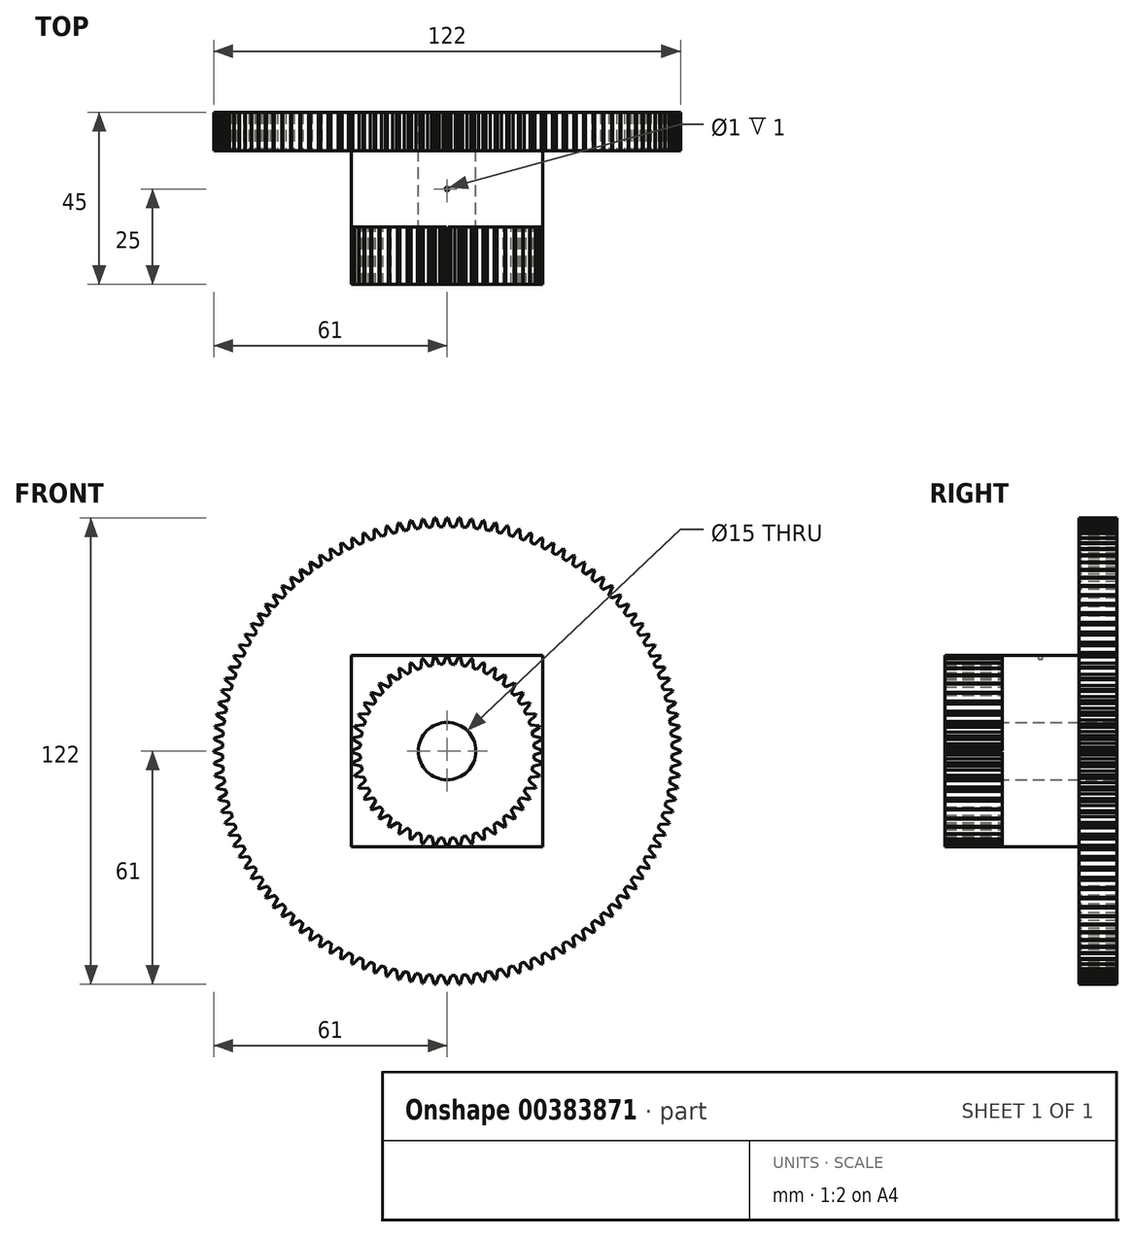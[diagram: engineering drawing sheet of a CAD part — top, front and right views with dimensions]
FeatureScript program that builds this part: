
annotation { "Feature Type Name" : "Feature", "Feature Type Description" : "" }
export const myFeature = defineFeature(function(context is Context, id is Id, definition is map)
    precondition{}
    {
        {
            var Q0;
            Q0=qCreatedBy(makeId("Front.planeOp"),FACE);
            var sketch = newSketch(context, id + "F0", { "sketchPlane" : qUnion([Q0])});
            skCircle(sketch, "E0", {"center": v(0, 0) * mm, "radius": 7.5 * mm});
            skCircle(sketch, "E1", {"center": v(0, 0) * mm, "radius": 22.75 * mm});
            skCircle(sketch, "E2", {"center": v(0, 0) * mm, "radius": 25 * mm, "construction": true});
            skLineSegment(sketch, "E3", {"start": v(-1.01, 22.73) * mm, "end": v(-0.19, 25) * mm});
            skLineSegment(sketch, "E4", {"start": v(-0.19, 25) * mm, "end": v(0, 25) * mm});
            skLineSegment(sketch, "E5", {"start": v(-1.01, 22.73) * mm, "end": v(-1.01, 25.94) * mm, "construction": true});
            skLineSegment(sketch, "E6.MirrorCS", {"start": v(0.19, 25) * mm, "end": v(0, 25) * mm});
            skLineSegment(sketch, "E7.MirrorCS", {"start": v(1.01, 22.73) * mm, "end": v(0.19, 25) * mm});
            skLineSegment(sketch, "E8.1.0", {"start": v(-3.97, 22.4) * mm, "end": v(-3.45, 24.76) * mm});
            skLineSegment(sketch, "E8.1.1", {"start": v(-3.45, 24.76) * mm, "end": v(-3.26, 24.79) * mm});
            skLineSegment(sketch, "E8.1.2", {"start": v(-3.08, 24.81) * mm, "end": v(-3.26, 24.79) * mm});
            skLineSegment(sketch, "E8.1.3", {"start": v(-1.96, 22.67) * mm, "end": v(-3.08, 24.81) * mm});
            skLineSegment(sketch, "E8.2.0", {"start": v(-6.86, 21.7) * mm, "end": v(-6.65, 24.1) * mm});
            skLineSegment(sketch, "E8.2.1", {"start": v(-6.65, 24.1) * mm, "end": v(-6.47, 24.15) * mm});
            skLineSegment(sketch, "E8.2.2", {"start": v(-6.29, 24.2) * mm, "end": v(-6.47, 24.15) * mm});
            skLineSegment(sketch, "E8.2.3", {"start": v(-4.9, 22.22) * mm, "end": v(-6.29, 24.2) * mm});
            skLineSegment(sketch, "E8.3.0", {"start": v(-9.63, 20.6) * mm, "end": v(-9.74, 23.03) * mm});
            skLineSegment(sketch, "E8.3.1", {"start": v(-9.74, 23.03) * mm, "end": v(-9.57, 23.1) * mm});
            skLineSegment(sketch, "E8.3.2", {"start": v(-9.4, 23.17) * mm, "end": v(-9.57, 23.1) * mm});
            skLineSegment(sketch, "E8.3.3", {"start": v(-7.76, 21.39) * mm, "end": v(-9.4, 23.17) * mm});
            skLineSegment(sketch, "E8.4.0", {"start": v(-12.24, 19.18) * mm, "end": v(-12.66, 21.56) * mm});
            skLineSegment(sketch, "E8.4.1", {"start": v(-12.66, 21.56) * mm, "end": v(-12.5, 21.65) * mm});
            skLineSegment(sketch, "E8.4.2", {"start": v(-12.34, 21.74) * mm, "end": v(-12.5, 21.65) * mm});
            skLineSegment(sketch, "E8.4.3", {"start": v(-10.48, 20.19) * mm, "end": v(-12.34, 21.74) * mm});
            skLineSegment(sketch, "E8.5.0", {"start": v(-14.64, 17.41) * mm, "end": v(-15.37, 19.72) * mm});
            skLineSegment(sketch, "E8.5.1", {"start": v(-15.37, 19.72) * mm, "end": v(-15.22, 19.83) * mm});
            skLineSegment(sketch, "E8.5.2", {"start": v(-15.07, 19.95) * mm, "end": v(-15.22, 19.83) * mm});
            skLineSegment(sketch, "E8.5.3", {"start": v(-13.03, 18.65) * mm, "end": v(-15.07, 19.95) * mm});
            skLineSegment(sketch, "E8.6.0", {"start": v(-16.79, 15.35) * mm, "end": v(-17.81, 17.55) * mm});
            skLineSegment(sketch, "E8.6.1", {"start": v(-17.81, 17.55) * mm, "end": v(-17.68, 17.68) * mm});
            skLineSegment(sketch, "E8.6.2", {"start": v(-17.55, 17.81) * mm, "end": v(-17.68, 17.68) * mm});
            skLineSegment(sketch, "E8.6.3", {"start": v(-15.35, 16.79) * mm, "end": v(-17.55, 17.81) * mm});
            skLineSegment(sketch, "E8.7.0", {"start": v(-18.65, 13.03) * mm, "end": v(-19.95, 15.07) * mm});
            skLineSegment(sketch, "E8.7.1", {"start": v(-19.95, 15.07) * mm, "end": v(-19.83, 15.22) * mm});
            skLineSegment(sketch, "E8.7.2", {"start": v(-19.72, 15.37) * mm, "end": v(-19.83, 15.22) * mm});
            skLineSegment(sketch, "E8.7.3", {"start": v(-17.41, 14.64) * mm, "end": v(-19.72, 15.37) * mm});
            skLineSegment(sketch, "E8.8.0", {"start": v(-20.19, 10.48) * mm, "end": v(-21.74, 12.34) * mm});
            skLineSegment(sketch, "E8.8.1", {"start": v(-21.74, 12.34) * mm, "end": v(-21.65, 12.5) * mm});
            skLineSegment(sketch, "E8.8.2", {"start": v(-21.56, 12.66) * mm, "end": v(-21.65, 12.5) * mm});
            skLineSegment(sketch, "E8.8.3", {"start": v(-19.18, 12.24) * mm, "end": v(-21.56, 12.66) * mm});
            skLineSegment(sketch, "E8.9.0", {"start": v(-21.39, 7.76) * mm, "end": v(-23.17, 9.4) * mm});
            skLineSegment(sketch, "E8.9.1", {"start": v(-23.17, 9.4) * mm, "end": v(-23.1, 9.57) * mm});
            skLineSegment(sketch, "E8.9.2", {"start": v(-23.03, 9.74) * mm, "end": v(-23.1, 9.57) * mm});
            skLineSegment(sketch, "E8.9.3", {"start": v(-20.6, 9.63) * mm, "end": v(-23.03, 9.74) * mm});
            skLineSegment(sketch, "E8.10.0", {"start": v(-22.22, 4.9) * mm, "end": v(-24.2, 6.29) * mm});
            skLineSegment(sketch, "E8.10.1", {"start": v(-24.2, 6.29) * mm, "end": v(-24.15, 6.47) * mm});
            skLineSegment(sketch, "E8.10.2", {"start": v(-24.1, 6.65) * mm, "end": v(-24.15, 6.47) * mm});
            skLineSegment(sketch, "E8.10.3", {"start": v(-21.7, 6.86) * mm, "end": v(-24.1, 6.65) * mm});
            skLineSegment(sketch, "E8.11.0", {"start": v(-22.67, 1.96) * mm, "end": v(-24.81, 3.08) * mm});
            skLineSegment(sketch, "E8.11.1", {"start": v(-24.81, 3.08) * mm, "end": v(-24.79, 3.26) * mm});
            skLineSegment(sketch, "E8.11.2", {"start": v(-24.76, 3.45) * mm, "end": v(-24.79, 3.26) * mm});
            skLineSegment(sketch, "E8.11.3", {"start": v(-22.4, 3.97) * mm, "end": v(-24.76, 3.45) * mm});
            skLineSegment(sketch, "E9.1.12.0", {"start": v(-22.73, -1.01) * mm, "end": v(-25, -0.19) * mm});
            skLineSegment(sketch, "E9.3.12.0", {"start": v(-25, -0.19) * mm, "end": v(-25, 0) * mm});
            skLineSegment(sketch, "E9.6.12.0", {"start": v(-25, 0.19) * mm, "end": v(-25, 0) * mm});
            skLineSegment(sketch, "E9.9.12.0", {"start": v(-22.73, 1.01) * mm, "end": v(-25, 0.19) * mm});
            skLineSegment(sketch, "E9.1.13.0", {"start": v(-22.4, -3.97) * mm, "end": v(-24.76, -3.45) * mm});
            skLineSegment(sketch, "E9.3.13.0", {"start": v(-24.76, -3.45) * mm, "end": v(-24.79, -3.26) * mm});
            skLineSegment(sketch, "E9.6.13.0", {"start": v(-24.81, -3.08) * mm, "end": v(-24.79, -3.26) * mm});
            skLineSegment(sketch, "E9.9.13.0", {"start": v(-22.67, -1.96) * mm, "end": v(-24.81, -3.08) * mm});
            skLineSegment(sketch, "E9.1.14.0", {"start": v(-21.7, -6.86) * mm, "end": v(-24.1, -6.65) * mm});
            skLineSegment(sketch, "E9.3.14.0", {"start": v(-24.1, -6.65) * mm, "end": v(-24.15, -6.47) * mm});
            skLineSegment(sketch, "E9.6.14.0", {"start": v(-24.2, -6.29) * mm, "end": v(-24.15, -6.47) * mm});
            skLineSegment(sketch, "E9.9.14.0", {"start": v(-22.22, -4.9) * mm, "end": v(-24.2, -6.29) * mm});
            skLineSegment(sketch, "E9.1.15.0", {"start": v(-20.6, -9.63) * mm, "end": v(-23.03, -9.74) * mm});
            skLineSegment(sketch, "E9.3.15.0", {"start": v(-23.03, -9.74) * mm, "end": v(-23.1, -9.57) * mm});
            skLineSegment(sketch, "E9.6.15.0", {"start": v(-23.17, -9.4) * mm, "end": v(-23.1, -9.57) * mm});
            skLineSegment(sketch, "E9.9.15.0", {"start": v(-21.39, -7.76) * mm, "end": v(-23.17, -9.4) * mm});
            skLineSegment(sketch, "E9.1.16.0", {"start": v(-19.18, -12.24) * mm, "end": v(-21.56, -12.66) * mm});
            skLineSegment(sketch, "E9.3.16.0", {"start": v(-21.56, -12.66) * mm, "end": v(-21.65, -12.5) * mm});
            skLineSegment(sketch, "E9.6.16.0", {"start": v(-21.74, -12.34) * mm, "end": v(-21.65, -12.5) * mm});
            skLineSegment(sketch, "E9.9.16.0", {"start": v(-20.19, -10.48) * mm, "end": v(-21.74, -12.34) * mm});
            skLineSegment(sketch, "E9.1.17.0", {"start": v(-17.41, -14.64) * mm, "end": v(-19.72, -15.37) * mm});
            skLineSegment(sketch, "E9.3.17.0", {"start": v(-19.72, -15.37) * mm, "end": v(-19.83, -15.22) * mm});
            skLineSegment(sketch, "E9.6.17.0", {"start": v(-19.95, -15.07) * mm, "end": v(-19.83, -15.22) * mm});
            skLineSegment(sketch, "E9.9.17.0", {"start": v(-18.65, -13.03) * mm, "end": v(-19.95, -15.07) * mm});
            skLineSegment(sketch, "E9.1.18.0", {"start": v(-15.35, -16.79) * mm, "end": v(-17.55, -17.81) * mm});
            skLineSegment(sketch, "E9.3.18.0", {"start": v(-17.55, -17.81) * mm, "end": v(-17.68, -17.68) * mm});
            skLineSegment(sketch, "E9.6.18.0", {"start": v(-17.81, -17.55) * mm, "end": v(-17.68, -17.68) * mm});
            skLineSegment(sketch, "E9.9.18.0", {"start": v(-16.79, -15.35) * mm, "end": v(-17.81, -17.55) * mm});
            skLineSegment(sketch, "E9.1.19.0", {"start": v(-13.03, -18.65) * mm, "end": v(-15.07, -19.95) * mm});
            skLineSegment(sketch, "E9.3.19.0", {"start": v(-15.07, -19.95) * mm, "end": v(-15.22, -19.83) * mm});
            skLineSegment(sketch, "E9.6.19.0", {"start": v(-15.37, -19.72) * mm, "end": v(-15.22, -19.83) * mm});
            skLineSegment(sketch, "E9.9.19.0", {"start": v(-14.64, -17.41) * mm, "end": v(-15.37, -19.72) * mm});
            skLineSegment(sketch, "E9.1.20.0", {"start": v(-10.48, -20.19) * mm, "end": v(-12.34, -21.74) * mm});
            skLineSegment(sketch, "E9.3.20.0", {"start": v(-12.34, -21.74) * mm, "end": v(-12.5, -21.65) * mm});
            skLineSegment(sketch, "E9.6.20.0", {"start": v(-12.66, -21.56) * mm, "end": v(-12.5, -21.65) * mm});
            skLineSegment(sketch, "E9.9.20.0", {"start": v(-12.24, -19.18) * mm, "end": v(-12.66, -21.56) * mm});
            skLineSegment(sketch, "E9.1.21.0", {"start": v(-7.76, -21.39) * mm, "end": v(-9.4, -23.17) * mm});
            skLineSegment(sketch, "E9.3.21.0", {"start": v(-9.4, -23.17) * mm, "end": v(-9.57, -23.1) * mm});
            skLineSegment(sketch, "E9.6.21.0", {"start": v(-9.74, -23.03) * mm, "end": v(-9.57, -23.1) * mm});
            skLineSegment(sketch, "E9.9.21.0", {"start": v(-9.63, -20.6) * mm, "end": v(-9.74, -23.03) * mm});
            skLineSegment(sketch, "E9.1.22.0", {"start": v(-4.9, -22.22) * mm, "end": v(-6.29, -24.2) * mm});
            skLineSegment(sketch, "E9.3.22.0", {"start": v(-6.29, -24.2) * mm, "end": v(-6.47, -24.15) * mm});
            skLineSegment(sketch, "E9.6.22.0", {"start": v(-6.65, -24.1) * mm, "end": v(-6.47, -24.15) * mm});
            skLineSegment(sketch, "E9.9.22.0", {"start": v(-6.86, -21.7) * mm, "end": v(-6.65, -24.1) * mm});
            skLineSegment(sketch, "E9.1.23.0", {"start": v(-1.96, -22.67) * mm, "end": v(-3.08, -24.81) * mm});
            skLineSegment(sketch, "E9.3.23.0", {"start": v(-3.08, -24.81) * mm, "end": v(-3.26, -24.79) * mm});
            skLineSegment(sketch, "E9.6.23.0", {"start": v(-3.45, -24.76) * mm, "end": v(-3.26, -24.79) * mm});
            skLineSegment(sketch, "E9.9.23.0", {"start": v(-3.97, -22.4) * mm, "end": v(-3.45, -24.76) * mm});
            skLineSegment(sketch, "E10.1.24.0", {"start": v(1.01, -22.73) * mm, "end": v(0.19, -25) * mm});
            skLineSegment(sketch, "E10.3.24.0", {"start": v(0.19, -25) * mm, "end": v(0, -25) * mm});
            skLineSegment(sketch, "E10.6.24.0", {"start": v(-0.19, -25) * mm, "end": v(0, -25) * mm});
            skLineSegment(sketch, "E10.9.24.0", {"start": v(-1.01, -22.73) * mm, "end": v(-0.19, -25) * mm});
            skLineSegment(sketch, "E10.1.25.0", {"start": v(3.97, -22.4) * mm, "end": v(3.45, -24.76) * mm});
            skLineSegment(sketch, "E10.3.25.0", {"start": v(3.45, -24.76) * mm, "end": v(3.26, -24.79) * mm});
            skLineSegment(sketch, "E10.6.25.0", {"start": v(3.08, -24.81) * mm, "end": v(3.26, -24.79) * mm});
            skLineSegment(sketch, "E10.9.25.0", {"start": v(1.96, -22.67) * mm, "end": v(3.08, -24.81) * mm});
            skLineSegment(sketch, "E10.1.26.0", {"start": v(6.86, -21.7) * mm, "end": v(6.65, -24.1) * mm});
            skLineSegment(sketch, "E10.3.26.0", {"start": v(6.65, -24.1) * mm, "end": v(6.47, -24.15) * mm});
            skLineSegment(sketch, "E10.6.26.0", {"start": v(6.29, -24.2) * mm, "end": v(6.47, -24.15) * mm});
            skLineSegment(sketch, "E10.9.26.0", {"start": v(4.9, -22.22) * mm, "end": v(6.29, -24.2) * mm});
            skLineSegment(sketch, "E10.1.27.0", {"start": v(9.63, -20.6) * mm, "end": v(9.74, -23.03) * mm});
            skLineSegment(sketch, "E10.3.27.0", {"start": v(9.74, -23.03) * mm, "end": v(9.57, -23.1) * mm});
            skLineSegment(sketch, "E10.6.27.0", {"start": v(9.4, -23.17) * mm, "end": v(9.57, -23.1) * mm});
            skLineSegment(sketch, "E10.9.27.0", {"start": v(7.76, -21.39) * mm, "end": v(9.4, -23.17) * mm});
            skLineSegment(sketch, "E10.1.28.0", {"start": v(12.24, -19.18) * mm, "end": v(12.66, -21.56) * mm});
            skLineSegment(sketch, "E10.3.28.0", {"start": v(12.66, -21.56) * mm, "end": v(12.5, -21.65) * mm});
            skLineSegment(sketch, "E10.6.28.0", {"start": v(12.34, -21.74) * mm, "end": v(12.5, -21.65) * mm});
            skLineSegment(sketch, "E10.9.28.0", {"start": v(10.48, -20.19) * mm, "end": v(12.34, -21.74) * mm});
            skLineSegment(sketch, "E10.1.29.0", {"start": v(14.64, -17.41) * mm, "end": v(15.37, -19.72) * mm});
            skLineSegment(sketch, "E10.3.29.0", {"start": v(15.37, -19.72) * mm, "end": v(15.22, -19.83) * mm});
            skLineSegment(sketch, "E10.6.29.0", {"start": v(15.07, -19.95) * mm, "end": v(15.22, -19.83) * mm});
            skLineSegment(sketch, "E10.9.29.0", {"start": v(13.03, -18.65) * mm, "end": v(15.07, -19.95) * mm});
            skLineSegment(sketch, "E10.1.30.0", {"start": v(16.79, -15.35) * mm, "end": v(17.81, -17.55) * mm});
            skLineSegment(sketch, "E10.3.30.0", {"start": v(17.81, -17.55) * mm, "end": v(17.68, -17.68) * mm});
            skLineSegment(sketch, "E10.6.30.0", {"start": v(17.55, -17.81) * mm, "end": v(17.68, -17.68) * mm});
            skLineSegment(sketch, "E10.9.30.0", {"start": v(15.35, -16.79) * mm, "end": v(17.55, -17.81) * mm});
            skLineSegment(sketch, "E10.1.31.0", {"start": v(18.65, -13.03) * mm, "end": v(19.95, -15.07) * mm});
            skLineSegment(sketch, "E10.3.31.0", {"start": v(19.95, -15.07) * mm, "end": v(19.83, -15.22) * mm});
            skLineSegment(sketch, "E10.6.31.0", {"start": v(19.72, -15.37) * mm, "end": v(19.83, -15.22) * mm});
            skLineSegment(sketch, "E10.9.31.0", {"start": v(17.41, -14.64) * mm, "end": v(19.72, -15.37) * mm});
            skLineSegment(sketch, "E10.1.32.0", {"start": v(20.19, -10.48) * mm, "end": v(21.74, -12.34) * mm});
            skLineSegment(sketch, "E10.3.32.0", {"start": v(21.74, -12.34) * mm, "end": v(21.65, -12.5) * mm});
            skLineSegment(sketch, "E10.6.32.0", {"start": v(21.56, -12.66) * mm, "end": v(21.65, -12.5) * mm});
            skLineSegment(sketch, "E10.9.32.0", {"start": v(19.18, -12.24) * mm, "end": v(21.56, -12.66) * mm});
            skLineSegment(sketch, "E10.1.33.0", {"start": v(21.39, -7.76) * mm, "end": v(23.17, -9.4) * mm});
            skLineSegment(sketch, "E10.3.33.0", {"start": v(23.17, -9.4) * mm, "end": v(23.1, -9.57) * mm});
            skLineSegment(sketch, "E10.6.33.0", {"start": v(23.03, -9.74) * mm, "end": v(23.1, -9.57) * mm});
            skLineSegment(sketch, "E10.9.33.0", {"start": v(20.6, -9.63) * mm, "end": v(23.03, -9.74) * mm});
            skLineSegment(sketch, "E10.1.34.0", {"start": v(22.22, -4.9) * mm, "end": v(24.2, -6.29) * mm});
            skLineSegment(sketch, "E10.3.34.0", {"start": v(24.2, -6.29) * mm, "end": v(24.15, -6.47) * mm});
            skLineSegment(sketch, "E10.6.34.0", {"start": v(24.1, -6.65) * mm, "end": v(24.15, -6.47) * mm});
            skLineSegment(sketch, "E10.9.34.0", {"start": v(21.7, -6.86) * mm, "end": v(24.1, -6.65) * mm});
            skLineSegment(sketch, "E10.1.35.0", {"start": v(22.67, -1.96) * mm, "end": v(24.81, -3.08) * mm});
            skLineSegment(sketch, "E10.3.35.0", {"start": v(24.81, -3.08) * mm, "end": v(24.79, -3.26) * mm});
            skLineSegment(sketch, "E10.6.35.0", {"start": v(24.76, -3.45) * mm, "end": v(24.79, -3.26) * mm});
            skLineSegment(sketch, "E10.9.35.0", {"start": v(22.4, -3.97) * mm, "end": v(24.76, -3.45) * mm});
            skLineSegment(sketch, "E11.1.36.0", {"start": v(22.73, 1.01) * mm, "end": v(25, 0.19) * mm});
            skLineSegment(sketch, "E11.3.36.0", {"start": v(25, 0.19) * mm, "end": v(25, 0) * mm});
            skLineSegment(sketch, "E11.6.36.0", {"start": v(25, -0.19) * mm, "end": v(25, 0) * mm});
            skLineSegment(sketch, "E11.9.36.0", {"start": v(22.73, -1.01) * mm, "end": v(25, -0.19) * mm});
            skLineSegment(sketch, "E11.1.37.0", {"start": v(22.4, 3.97) * mm, "end": v(24.76, 3.45) * mm});
            skLineSegment(sketch, "E11.3.37.0", {"start": v(24.76, 3.45) * mm, "end": v(24.79, 3.26) * mm});
            skLineSegment(sketch, "E11.6.37.0", {"start": v(24.81, 3.08) * mm, "end": v(24.79, 3.26) * mm});
            skLineSegment(sketch, "E11.9.37.0", {"start": v(22.67, 1.96) * mm, "end": v(24.81, 3.08) * mm});
            skLineSegment(sketch, "E11.1.38.0", {"start": v(21.7, 6.86) * mm, "end": v(24.1, 6.65) * mm});
            skLineSegment(sketch, "E11.3.38.0", {"start": v(24.1, 6.65) * mm, "end": v(24.15, 6.47) * mm});
            skLineSegment(sketch, "E11.6.38.0", {"start": v(24.2, 6.29) * mm, "end": v(24.15, 6.47) * mm});
            skLineSegment(sketch, "E11.9.38.0", {"start": v(22.22, 4.9) * mm, "end": v(24.2, 6.29) * mm});
            skLineSegment(sketch, "E11.1.39.0", {"start": v(20.6, 9.63) * mm, "end": v(23.03, 9.74) * mm});
            skLineSegment(sketch, "E11.3.39.0", {"start": v(23.03, 9.74) * mm, "end": v(23.1, 9.57) * mm});
            skLineSegment(sketch, "E11.6.39.0", {"start": v(23.17, 9.4) * mm, "end": v(23.1, 9.57) * mm});
            skLineSegment(sketch, "E11.9.39.0", {"start": v(21.39, 7.76) * mm, "end": v(23.17, 9.4) * mm});
            skLineSegment(sketch, "E11.1.40.0", {"start": v(19.18, 12.24) * mm, "end": v(21.56, 12.66) * mm});
            skLineSegment(sketch, "E11.3.40.0", {"start": v(21.56, 12.66) * mm, "end": v(21.65, 12.5) * mm});
            skLineSegment(sketch, "E11.6.40.0", {"start": v(21.74, 12.34) * mm, "end": v(21.65, 12.5) * mm});
            skLineSegment(sketch, "E11.9.40.0", {"start": v(20.19, 10.48) * mm, "end": v(21.74, 12.34) * mm});
            skLineSegment(sketch, "E11.1.41.0", {"start": v(17.41, 14.64) * mm, "end": v(19.72, 15.37) * mm});
            skLineSegment(sketch, "E11.3.41.0", {"start": v(19.72, 15.37) * mm, "end": v(19.83, 15.22) * mm});
            skLineSegment(sketch, "E11.6.41.0", {"start": v(19.95, 15.07) * mm, "end": v(19.83, 15.22) * mm});
            skLineSegment(sketch, "E11.9.41.0", {"start": v(18.65, 13.03) * mm, "end": v(19.95, 15.07) * mm});
            skLineSegment(sketch, "E11.1.42.0", {"start": v(15.35, 16.79) * mm, "end": v(17.55, 17.81) * mm});
            skLineSegment(sketch, "E11.3.42.0", {"start": v(17.55, 17.81) * mm, "end": v(17.68, 17.68) * mm});
            skLineSegment(sketch, "E11.6.42.0", {"start": v(17.81, 17.55) * mm, "end": v(17.68, 17.68) * mm});
            skLineSegment(sketch, "E11.9.42.0", {"start": v(16.79, 15.35) * mm, "end": v(17.81, 17.55) * mm});
            skLineSegment(sketch, "E11.1.43.0", {"start": v(13.03, 18.65) * mm, "end": v(15.07, 19.95) * mm});
            skLineSegment(sketch, "E11.3.43.0", {"start": v(15.07, 19.95) * mm, "end": v(15.22, 19.83) * mm});
            skLineSegment(sketch, "E11.6.43.0", {"start": v(15.37, 19.72) * mm, "end": v(15.22, 19.83) * mm});
            skLineSegment(sketch, "E11.9.43.0", {"start": v(14.64, 17.41) * mm, "end": v(15.37, 19.72) * mm});
            skLineSegment(sketch, "E11.1.44.0", {"start": v(10.48, 20.19) * mm, "end": v(12.34, 21.74) * mm});
            skLineSegment(sketch, "E11.3.44.0", {"start": v(12.34, 21.74) * mm, "end": v(12.5, 21.65) * mm});
            skLineSegment(sketch, "E11.6.44.0", {"start": v(12.66, 21.56) * mm, "end": v(12.5, 21.65) * mm});
            skLineSegment(sketch, "E11.9.44.0", {"start": v(12.24, 19.18) * mm, "end": v(12.66, 21.56) * mm});
            skLineSegment(sketch, "E11.1.45.0", {"start": v(7.76, 21.39) * mm, "end": v(9.4, 23.17) * mm});
            skLineSegment(sketch, "E11.3.45.0", {"start": v(9.4, 23.17) * mm, "end": v(9.57, 23.1) * mm});
            skLineSegment(sketch, "E11.6.45.0", {"start": v(9.74, 23.03) * mm, "end": v(9.57, 23.1) * mm});
            skLineSegment(sketch, "E11.9.45.0", {"start": v(9.63, 20.6) * mm, "end": v(9.74, 23.03) * mm});
            skLineSegment(sketch, "E11.1.46.0", {"start": v(4.9, 22.22) * mm, "end": v(6.29, 24.2) * mm});
            skLineSegment(sketch, "E11.3.46.0", {"start": v(6.29, 24.2) * mm, "end": v(6.47, 24.15) * mm});
            skLineSegment(sketch, "E11.6.46.0", {"start": v(6.65, 24.1) * mm, "end": v(6.47, 24.15) * mm});
            skLineSegment(sketch, "E11.9.46.0", {"start": v(6.86, 21.7) * mm, "end": v(6.65, 24.1) * mm});
            skLineSegment(sketch, "E11.1.47.0", {"start": v(1.96, 22.67) * mm, "end": v(3.08, 24.81) * mm});
            skLineSegment(sketch, "E11.3.47.0", {"start": v(3.08, 24.81) * mm, "end": v(3.26, 24.79) * mm});
            skLineSegment(sketch, "E11.6.47.0", {"start": v(3.45, 24.76) * mm, "end": v(3.26, 24.79) * mm});
            skLineSegment(sketch, "E11.9.47.0", {"start": v(3.97, 22.4) * mm, "end": v(3.45, 24.76) * mm});
            skSolve(sketch);
        }
        {
            var Q0;
            Q0=qSketchRegion(id+"F0",true);
            extrude(context, id + "F1", {"entities" : qUnion([Q0]), "depth" : 15 * mm});
        }
        {
            var Q0;
            Q0=qCreatedBy(makeId("Front.planeOp"),FACE);
            var sketch = newSketch(context, id + "F2", { "sketchPlane" : qUnion([Q0])});
            skCircle(sketch, "E12", {"center": v(0, 0) * mm, "radius": 7.5 * mm});
            skLineSegment(sketch, "E13.bottom", {"start": v(-25, -25) * mm, "end": v(25, -25) * mm});
            skLineSegment(sketch, "E13.top", {"start": v(-25, 25) * mm, "end": v(25, 25) * mm});
            skLineSegment(sketch, "E13.left", {"start": v(-25, -25) * mm, "end": v(-25, 25) * mm});
            skLineSegment(sketch, "E13.right", {"start": v(25, -25) * mm, "end": v(25, 25) * mm});
            skSolve(sketch);
        }
        {
            var Q0;
            Q0=qSketchRegion(id+"F2",true);
            extrude(context, id + "F3", {"entities" : qUnion([Q0]), "operationType" : NewBodyOperationType.ADD, "depth" : -20 * mm});
        }
        {
            var Q0;
            Q0=makeQuery(id+"F3.opExtrude","CAP_FACE",FACE,{"disambiguationData":[OSD([sQuery(id+"F2.wireOp",EDGE,"Zh5lLQ9h-1iR5-KiPg-C2Wr-JR3NM9Zv75rL"),sQuery(id+"F2.wireOp",EDGE,"E12")])],"isStart":false});
            var sketch = newSketch(context, id + "F4", { "sketchPlane" : qUnion([Q0])});
            skCircle(sketch, "E14", {"center": v(0, 0) * mm, "radius": 58.75 * mm});
            skCircle(sketch, "E15", {"center": v(0, 0) * mm, "radius": 61 * mm, "construction": true});
            skLineSegment(sketch, "E16", {"start": v(-1, 58.74) * mm, "end": v(-1, 64.16) * mm, "construction": true});
            skLineSegment(sketch, "E17", {"start": v(-1, 58.74) * mm, "end": v(-0.19, 61) * mm});
            skLineSegment(sketch, "E18", {"start": v(-0.19, 61) * mm, "end": v(0, 61) * mm});
            skLineSegment(sketch, "E19.MirrorCS", {"start": v(0.19, 61) * mm, "end": v(0, 61) * mm});
            skLineSegment(sketch, "E20.MirrorCS", {"start": v(1, 58.74) * mm, "end": v(0.19, 61) * mm});
            skLineSegment(sketch, "E21.1.0", {"start": v(-4.08, 58.6) * mm, "end": v(-3.38, 60.9) * mm});
            skLineSegment(sketch, "E21.1.1", {"start": v(-3.38, 60.9) * mm, "end": v(-3.2, 60.92) * mm});
            skLineSegment(sketch, "E21.1.2", {"start": v(-3, 60.93) * mm, "end": v(-3.2, 60.92) * mm});
            skLineSegment(sketch, "E21.1.3", {"start": v(-2.07, 58.71) * mm, "end": v(-3, 60.93) * mm});
            skLineSegment(sketch, "E21.2.0", {"start": v(-7.14, 58.31) * mm, "end": v(-6.56, 60.65) * mm});
            skLineSegment(sketch, "E21.2.1", {"start": v(-6.56, 60.65) * mm, "end": v(-6.38, 60.67) * mm});
            skLineSegment(sketch, "E21.2.2", {"start": v(-6.19, 60.69) * mm, "end": v(-6.38, 60.67) * mm});
            skLineSegment(sketch, "E21.2.3", {"start": v(-5.14, 58.53) * mm, "end": v(-6.19, 60.69) * mm});
            skLineSegment(sketch, "E21.3.0", {"start": v(-10.19, 57.86) * mm, "end": v(-9.73, 60.22) * mm});
            skLineSegment(sketch, "E21.3.1", {"start": v(-9.73, 60.22) * mm, "end": v(-9.54, 60.25) * mm});
            skLineSegment(sketch, "E21.3.2", {"start": v(-9.36, 60.28) * mm, "end": v(-9.54, 60.25) * mm});
            skLineSegment(sketch, "E21.3.3", {"start": v(-8.2, 58.18) * mm, "end": v(-9.36, 60.28) * mm});
            skLineSegment(sketch, "E21.4.0", {"start": v(-13.2, 57.25) * mm, "end": v(-12.87, 59.63) * mm});
            skLineSegment(sketch, "E21.4.1", {"start": v(-12.87, 59.63) * mm, "end": v(-12.68, 59.67) * mm});
            skLineSegment(sketch, "E21.4.2", {"start": v(-12.5, 59.7) * mm, "end": v(-12.68, 59.67) * mm});
            skLineSegment(sketch, "E21.4.3", {"start": v(-11.23, 57.67) * mm, "end": v(-12.5, 59.7) * mm});
            skLineSegment(sketch, "E21.5.0", {"start": v(-16.18, 56.48) * mm, "end": v(-15.97, 58.87) * mm});
            skLineSegment(sketch, "E21.5.1", {"start": v(-15.97, 58.87) * mm, "end": v(-15.79, 58.92) * mm});
            skLineSegment(sketch, "E21.5.2", {"start": v(-15.6, 58.97) * mm, "end": v(-15.79, 58.92) * mm});
            skLineSegment(sketch, "E21.5.3", {"start": v(-14.23, 57) * mm, "end": v(-15.6, 58.97) * mm});
            skLineSegment(sketch, "E21.6.0", {"start": v(-19.11, 55.55) * mm, "end": v(-19.03, 57.96) * mm});
            skLineSegment(sketch, "E21.6.1", {"start": v(-19.03, 57.96) * mm, "end": v(-18.85, 58.01) * mm});
            skLineSegment(sketch, "E21.6.2", {"start": v(-18.67, 58.07) * mm, "end": v(-18.85, 58.01) * mm});
            skLineSegment(sketch, "E21.6.3", {"start": v(-17.2, 56.18) * mm, "end": v(-18.67, 58.07) * mm});
            skLineSegment(sketch, "E21.7.0", {"start": v(-22, 54.48) * mm, "end": v(-22.04, 56.88) * mm});
            skLineSegment(sketch, "E21.7.1", {"start": v(-22.04, 56.88) * mm, "end": v(-21.86, 56.95) * mm});
            skLineSegment(sketch, "E21.7.2", {"start": v(-21.69, 57.02) * mm, "end": v(-21.86, 56.95) * mm});
            skLineSegment(sketch, "E21.7.3", {"start": v(-20.1, 55.2) * mm, "end": v(-21.69, 57.02) * mm});
            skLineSegment(sketch, "E21.8.0", {"start": v(-24.81, 53.25) * mm, "end": v(-24.98, 55.65) * mm});
            skLineSegment(sketch, "E21.8.1", {"start": v(-24.98, 55.65) * mm, "end": v(-24.81, 55.73) * mm});
            skLineSegment(sketch, "E21.8.2", {"start": v(-24.64, 55.8) * mm, "end": v(-24.81, 55.73) * mm});
            skLineSegment(sketch, "E21.8.3", {"start": v(-22.97, 54.07) * mm, "end": v(-24.64, 55.8) * mm});
            skLineSegment(sketch, "E21.9.0", {"start": v(-27.57, 51.88) * mm, "end": v(-27.86, 54.27) * mm});
            skLineSegment(sketch, "E21.9.1", {"start": v(-27.86, 54.27) * mm, "end": v(-27.7, 54.35) * mm});
            skLineSegment(sketch, "E21.9.2", {"start": v(-27.53, 54.44) * mm, "end": v(-27.7, 54.35) * mm});
            skLineSegment(sketch, "E21.9.3", {"start": v(-25.77, 52.8) * mm, "end": v(-27.53, 54.44) * mm});
            skLineSegment(sketch, "E21.10.0", {"start": v(-30.24, 50.37) * mm, "end": v(-30.66, 52.73) * mm});
            skLineSegment(sketch, "E21.10.1", {"start": v(-30.66, 52.73) * mm, "end": v(-30.5, 52.83) * mm});
            skLineSegment(sketch, "E21.10.2", {"start": v(-30.34, 52.92) * mm, "end": v(-30.5, 52.83) * mm});
            skLineSegment(sketch, "E21.10.3", {"start": v(-28.5, 51.38) * mm, "end": v(-30.34, 52.92) * mm});
            skLineSegment(sketch, "E21.11.0", {"start": v(-32.84, 48.71) * mm, "end": v(-33.38, 51.06) * mm});
            skLineSegment(sketch, "E21.11.1", {"start": v(-33.38, 51.06) * mm, "end": v(-33.22, 51.16) * mm});
            skLineSegment(sketch, "E21.11.2", {"start": v(-33.07, 51.26) * mm, "end": v(-33.22, 51.16) * mm});
            skLineSegment(sketch, "E21.11.3", {"start": v(-31.15, 49.81) * mm, "end": v(-33.07, 51.26) * mm});
            skLineSegment(sketch, "E21.12.0", {"start": v(-35.34, 46.93) * mm, "end": v(-36, 49.24) * mm});
            skLineSegment(sketch, "E21.12.1", {"start": v(-36, 49.24) * mm, "end": v(-35.85, 49.35) * mm});
            skLineSegment(sketch, "E21.12.2", {"start": v(-35.7, 49.46) * mm, "end": v(-35.85, 49.35) * mm});
            skLineSegment(sketch, "E21.12.3", {"start": v(-33.71, 48.12) * mm, "end": v(-35.7, 49.46) * mm});
            skLineSegment(sketch, "E21.13.0", {"start": v(-37.75, 45.02) * mm, "end": v(-38.53, 47.29) * mm});
            skLineSegment(sketch, "E21.13.1", {"start": v(-38.53, 47.29) * mm, "end": v(-38.39, 47.4) * mm});
            skLineSegment(sketch, "E21.13.2", {"start": v(-38.24, 47.52) * mm, "end": v(-38.39, 47.4) * mm});
            skLineSegment(sketch, "E21.13.3", {"start": v(-36.18, 46.29) * mm, "end": v(-38.24, 47.52) * mm});
            skLineSegment(sketch, "E21.14.0", {"start": v(-40.06, 42.98) * mm, "end": v(-40.96, 45.2) * mm});
            skLineSegment(sketch, "E21.14.1", {"start": v(-40.96, 45.2) * mm, "end": v(-40.82, 45.33) * mm});
            skLineSegment(sketch, "E21.14.2", {"start": v(-40.68, 45.46) * mm, "end": v(-40.82, 45.33) * mm});
            skLineSegment(sketch, "E21.14.3", {"start": v(-38.56, 44.33) * mm, "end": v(-40.68, 45.46) * mm});
            skLineSegment(sketch, "E21.15.0", {"start": v(-42.25, 40.82) * mm, "end": v(-43.27, 43) * mm});
            skLineSegment(sketch, "E21.15.1", {"start": v(-43.27, 43) * mm, "end": v(-43.13, 43.13) * mm});
            skLineSegment(sketch, "E21.15.2", {"start": v(-43, 43.27) * mm, "end": v(-43.13, 43.13) * mm});
            skLineSegment(sketch, "E21.15.3", {"start": v(-40.82, 42.25) * mm, "end": v(-43, 43.27) * mm});
            skLineSegment(sketch, "E21.16.0", {"start": v(-44.33, 38.56) * mm, "end": v(-45.46, 40.68) * mm});
            skLineSegment(sketch, "E21.16.1", {"start": v(-45.46, 40.68) * mm, "end": v(-45.33, 40.82) * mm});
            skLineSegment(sketch, "E21.16.2", {"start": v(-45.2, 40.96) * mm, "end": v(-45.33, 40.82) * mm});
            skLineSegment(sketch, "E21.16.3", {"start": v(-42.98, 40.06) * mm, "end": v(-45.2, 40.96) * mm});
            skLineSegment(sketch, "E21.17.0", {"start": v(-46.29, 36.18) * mm, "end": v(-47.52, 38.24) * mm});
            skLineSegment(sketch, "E21.17.1", {"start": v(-47.52, 38.24) * mm, "end": v(-47.4, 38.39) * mm});
            skLineSegment(sketch, "E21.17.2", {"start": v(-47.29, 38.53) * mm, "end": v(-47.4, 38.39) * mm});
            skLineSegment(sketch, "E21.17.3", {"start": v(-45.02, 37.75) * mm, "end": v(-47.29, 38.53) * mm});
            skLineSegment(sketch, "E21.18.0", {"start": v(-48.12, 33.71) * mm, "end": v(-49.46, 35.7) * mm});
            skLineSegment(sketch, "E21.18.1", {"start": v(-49.46, 35.7) * mm, "end": v(-49.35, 35.85) * mm});
            skLineSegment(sketch, "E21.18.2", {"start": v(-49.24, 36) * mm, "end": v(-49.35, 35.85) * mm});
            skLineSegment(sketch, "E21.18.3", {"start": v(-46.93, 35.34) * mm, "end": v(-49.24, 36) * mm});
            skLineSegment(sketch, "E21.19.0", {"start": v(-49.81, 31.15) * mm, "end": v(-51.26, 33.07) * mm});
            skLineSegment(sketch, "E21.19.1", {"start": v(-51.26, 33.07) * mm, "end": v(-51.16, 33.22) * mm});
            skLineSegment(sketch, "E21.19.2", {"start": v(-51.06, 33.38) * mm, "end": v(-51.16, 33.22) * mm});
            skLineSegment(sketch, "E21.19.3", {"start": v(-48.71, 32.84) * mm, "end": v(-51.06, 33.38) * mm});
            skLineSegment(sketch, "E21.20.0", {"start": v(-51.38, 28.5) * mm, "end": v(-52.92, 30.34) * mm});
            skLineSegment(sketch, "E21.20.1", {"start": v(-52.92, 30.34) * mm, "end": v(-52.83, 30.5) * mm});
            skLineSegment(sketch, "E21.20.2", {"start": v(-52.73, 30.66) * mm, "end": v(-52.83, 30.5) * mm});
            skLineSegment(sketch, "E21.20.3", {"start": v(-50.37, 30.24) * mm, "end": v(-52.73, 30.66) * mm});
            skLineSegment(sketch, "E21.21.0", {"start": v(-52.8, 25.77) * mm, "end": v(-54.44, 27.53) * mm});
            skLineSegment(sketch, "E21.21.1", {"start": v(-54.44, 27.53) * mm, "end": v(-54.35, 27.7) * mm});
            skLineSegment(sketch, "E21.21.2", {"start": v(-54.27, 27.86) * mm, "end": v(-54.35, 27.7) * mm});
            skLineSegment(sketch, "E21.21.3", {"start": v(-51.88, 27.57) * mm, "end": v(-54.27, 27.86) * mm});
            skLineSegment(sketch, "E21.22.0", {"start": v(-54.07, 22.97) * mm, "end": v(-55.8, 24.64) * mm});
            skLineSegment(sketch, "E21.22.1", {"start": v(-55.8, 24.64) * mm, "end": v(-55.73, 24.81) * mm});
            skLineSegment(sketch, "E21.22.2", {"start": v(-55.65, 24.98) * mm, "end": v(-55.73, 24.81) * mm});
            skLineSegment(sketch, "E21.22.3", {"start": v(-53.25, 24.81) * mm, "end": v(-55.65, 24.98) * mm});
            skLineSegment(sketch, "E21.23.0", {"start": v(-55.2, 20.1) * mm, "end": v(-57.02, 21.69) * mm});
            skLineSegment(sketch, "E21.23.1", {"start": v(-57.02, 21.69) * mm, "end": v(-56.95, 21.86) * mm});
            skLineSegment(sketch, "E21.23.2", {"start": v(-56.88, 22.04) * mm, "end": v(-56.95, 21.86) * mm});
            skLineSegment(sketch, "E21.23.3", {"start": v(-54.48, 22) * mm, "end": v(-56.88, 22.04) * mm});
            skLineSegment(sketch, "E21.24.0", {"start": v(-56.18, 17.2) * mm, "end": v(-58.07, 18.67) * mm});
            skLineSegment(sketch, "E21.24.1", {"start": v(-58.07, 18.67) * mm, "end": v(-58.01, 18.85) * mm});
            skLineSegment(sketch, "E21.24.2", {"start": v(-57.96, 19.03) * mm, "end": v(-58.01, 18.85) * mm});
            skLineSegment(sketch, "E21.24.3", {"start": v(-55.55, 19.11) * mm, "end": v(-57.96, 19.03) * mm});
            skLineSegment(sketch, "E21.25.0", {"start": v(-57, 14.23) * mm, "end": v(-58.97, 15.6) * mm});
            skLineSegment(sketch, "E21.25.1", {"start": v(-58.97, 15.6) * mm, "end": v(-58.92, 15.79) * mm});
            skLineSegment(sketch, "E21.25.2", {"start": v(-58.87, 15.97) * mm, "end": v(-58.92, 15.79) * mm});
            skLineSegment(sketch, "E21.25.3", {"start": v(-56.48, 16.18) * mm, "end": v(-58.87, 15.97) * mm});
            skLineSegment(sketch, "E21.26.0", {"start": v(-57.67, 11.23) * mm, "end": v(-59.7, 12.5) * mm});
            skLineSegment(sketch, "E21.26.1", {"start": v(-59.7, 12.5) * mm, "end": v(-59.67, 12.68) * mm});
            skLineSegment(sketch, "E21.26.2", {"start": v(-59.63, 12.87) * mm, "end": v(-59.67, 12.68) * mm});
            skLineSegment(sketch, "E21.26.3", {"start": v(-57.25, 13.2) * mm, "end": v(-59.63, 12.87) * mm});
            skLineSegment(sketch, "E21.27.0", {"start": v(-58.18, 8.2) * mm, "end": v(-60.28, 9.36) * mm});
            skLineSegment(sketch, "E21.27.1", {"start": v(-60.28, 9.36) * mm, "end": v(-60.25, 9.54) * mm});
            skLineSegment(sketch, "E21.27.2", {"start": v(-60.22, 9.73) * mm, "end": v(-60.25, 9.54) * mm});
            skLineSegment(sketch, "E21.27.3", {"start": v(-57.86, 10.19) * mm, "end": v(-60.22, 9.73) * mm});
            skLineSegment(sketch, "E21.28.0", {"start": v(-58.53, 5.14) * mm, "end": v(-60.69, 6.19) * mm});
            skLineSegment(sketch, "E21.28.1", {"start": v(-60.69, 6.19) * mm, "end": v(-60.67, 6.38) * mm});
            skLineSegment(sketch, "E21.28.2", {"start": v(-60.65, 6.56) * mm, "end": v(-60.67, 6.38) * mm});
            skLineSegment(sketch, "E21.28.3", {"start": v(-58.31, 7.14) * mm, "end": v(-60.65, 6.56) * mm});
            skLineSegment(sketch, "E21.29.0", {"start": v(-58.71, 2.07) * mm, "end": v(-60.93, 3) * mm});
            skLineSegment(sketch, "E21.29.1", {"start": v(-60.93, 3) * mm, "end": v(-60.92, 3.2) * mm});
            skLineSegment(sketch, "E21.29.2", {"start": v(-60.9, 3.38) * mm, "end": v(-60.92, 3.2) * mm});
            skLineSegment(sketch, "E21.29.3", {"start": v(-58.6, 4.08) * mm, "end": v(-60.9, 3.38) * mm});
            skLineSegment(sketch, "E21.30.0", {"start": v(-58.74, -1) * mm, "end": v(-61, -0.19) * mm});
            skLineSegment(sketch, "E21.30.1", {"start": v(-61, -0.19) * mm, "end": v(-61, 0) * mm});
            skLineSegment(sketch, "E21.30.2", {"start": v(-61, 0.19) * mm, "end": v(-61, 0) * mm});
            skLineSegment(sketch, "E21.30.3", {"start": v(-58.74, 1) * mm, "end": v(-61, 0.19) * mm});
            skLineSegment(sketch, "E21.31.0", {"start": v(-58.6, -4.08) * mm, "end": v(-60.9, -3.38) * mm});
            skLineSegment(sketch, "E21.31.1", {"start": v(-60.9, -3.38) * mm, "end": v(-60.92, -3.2) * mm});
            skLineSegment(sketch, "E21.31.2", {"start": v(-60.93, -3) * mm, "end": v(-60.92, -3.2) * mm});
            skLineSegment(sketch, "E21.31.3", {"start": v(-58.71, -2.07) * mm, "end": v(-60.93, -3) * mm});
            skLineSegment(sketch, "E21.32.0", {"start": v(-58.31, -7.14) * mm, "end": v(-60.65, -6.56) * mm});
            skLineSegment(sketch, "E21.32.1", {"start": v(-60.65, -6.56) * mm, "end": v(-60.67, -6.38) * mm});
            skLineSegment(sketch, "E21.32.2", {"start": v(-60.69, -6.19) * mm, "end": v(-60.67, -6.38) * mm});
            skLineSegment(sketch, "E21.32.3", {"start": v(-58.53, -5.14) * mm, "end": v(-60.69, -6.19) * mm});
            skLineSegment(sketch, "E21.33.0", {"start": v(-57.86, -10.19) * mm, "end": v(-60.22, -9.73) * mm});
            skLineSegment(sketch, "E21.33.1", {"start": v(-60.22, -9.73) * mm, "end": v(-60.25, -9.54) * mm});
            skLineSegment(sketch, "E21.33.2", {"start": v(-60.28, -9.36) * mm, "end": v(-60.25, -9.54) * mm});
            skLineSegment(sketch, "E21.33.3", {"start": v(-58.18, -8.2) * mm, "end": v(-60.28, -9.36) * mm});
            skLineSegment(sketch, "E21.34.0", {"start": v(-57.25, -13.2) * mm, "end": v(-59.63, -12.87) * mm});
            skLineSegment(sketch, "E21.34.1", {"start": v(-59.63, -12.87) * mm, "end": v(-59.67, -12.68) * mm});
            skLineSegment(sketch, "E21.34.2", {"start": v(-59.7, -12.5) * mm, "end": v(-59.67, -12.68) * mm});
            skLineSegment(sketch, "E21.34.3", {"start": v(-57.67, -11.23) * mm, "end": v(-59.7, -12.5) * mm});
            skLineSegment(sketch, "E21.35.0", {"start": v(-56.48, -16.18) * mm, "end": v(-58.87, -15.97) * mm});
            skLineSegment(sketch, "E21.35.1", {"start": v(-58.87, -15.97) * mm, "end": v(-58.92, -15.79) * mm});
            skLineSegment(sketch, "E21.35.2", {"start": v(-58.97, -15.6) * mm, "end": v(-58.92, -15.79) * mm});
            skLineSegment(sketch, "E21.35.3", {"start": v(-57, -14.23) * mm, "end": v(-58.97, -15.6) * mm});
            skLineSegment(sketch, "E21.36.0", {"start": v(-55.55, -19.11) * mm, "end": v(-57.96, -19.03) * mm});
            skLineSegment(sketch, "E21.36.1", {"start": v(-57.96, -19.03) * mm, "end": v(-58.01, -18.85) * mm});
            skLineSegment(sketch, "E21.36.2", {"start": v(-58.07, -18.67) * mm, "end": v(-58.01, -18.85) * mm});
            skLineSegment(sketch, "E21.36.3", {"start": v(-56.18, -17.2) * mm, "end": v(-58.07, -18.67) * mm});
            skLineSegment(sketch, "E21.37.0", {"start": v(-54.48, -22) * mm, "end": v(-56.88, -22.04) * mm});
            skLineSegment(sketch, "E21.37.1", {"start": v(-56.88, -22.04) * mm, "end": v(-56.95, -21.86) * mm});
            skLineSegment(sketch, "E21.37.2", {"start": v(-57.02, -21.69) * mm, "end": v(-56.95, -21.86) * mm});
            skLineSegment(sketch, "E21.37.3", {"start": v(-55.2, -20.1) * mm, "end": v(-57.02, -21.69) * mm});
            skLineSegment(sketch, "E21.38.0", {"start": v(-53.25, -24.81) * mm, "end": v(-55.65, -24.98) * mm});
            skLineSegment(sketch, "E21.38.1", {"start": v(-55.65, -24.98) * mm, "end": v(-55.73, -24.81) * mm});
            skLineSegment(sketch, "E21.38.2", {"start": v(-55.8, -24.64) * mm, "end": v(-55.73, -24.81) * mm});
            skLineSegment(sketch, "E21.38.3", {"start": v(-54.07, -22.97) * mm, "end": v(-55.8, -24.64) * mm});
            skLineSegment(sketch, "E21.39.0", {"start": v(-51.88, -27.57) * mm, "end": v(-54.27, -27.86) * mm});
            skLineSegment(sketch, "E21.39.1", {"start": v(-54.27, -27.86) * mm, "end": v(-54.35, -27.7) * mm});
            skLineSegment(sketch, "E21.39.2", {"start": v(-54.44, -27.53) * mm, "end": v(-54.35, -27.7) * mm});
            skLineSegment(sketch, "E21.39.3", {"start": v(-52.8, -25.77) * mm, "end": v(-54.44, -27.53) * mm});
            skLineSegment(sketch, "E21.40.0", {"start": v(-50.37, -30.24) * mm, "end": v(-52.73, -30.66) * mm});
            skLineSegment(sketch, "E21.40.1", {"start": v(-52.73, -30.66) * mm, "end": v(-52.83, -30.5) * mm});
            skLineSegment(sketch, "E21.40.2", {"start": v(-52.92, -30.34) * mm, "end": v(-52.83, -30.5) * mm});
            skLineSegment(sketch, "E21.40.3", {"start": v(-51.38, -28.5) * mm, "end": v(-52.92, -30.34) * mm});
            skLineSegment(sketch, "E21.41.0", {"start": v(-48.71, -32.84) * mm, "end": v(-51.06, -33.38) * mm});
            skLineSegment(sketch, "E21.41.1", {"start": v(-51.06, -33.38) * mm, "end": v(-51.16, -33.22) * mm});
            skLineSegment(sketch, "E21.41.2", {"start": v(-51.26, -33.07) * mm, "end": v(-51.16, -33.22) * mm});
            skLineSegment(sketch, "E21.41.3", {"start": v(-49.81, -31.15) * mm, "end": v(-51.26, -33.07) * mm});
            skLineSegment(sketch, "E21.42.0", {"start": v(-46.93, -35.34) * mm, "end": v(-49.24, -36) * mm});
            skLineSegment(sketch, "E21.42.1", {"start": v(-49.24, -36) * mm, "end": v(-49.35, -35.85) * mm});
            skLineSegment(sketch, "E21.42.2", {"start": v(-49.46, -35.7) * mm, "end": v(-49.35, -35.85) * mm});
            skLineSegment(sketch, "E21.42.3", {"start": v(-48.12, -33.71) * mm, "end": v(-49.46, -35.7) * mm});
            skLineSegment(sketch, "E21.43.0", {"start": v(-45.02, -37.75) * mm, "end": v(-47.29, -38.53) * mm});
            skLineSegment(sketch, "E21.43.1", {"start": v(-47.29, -38.53) * mm, "end": v(-47.4, -38.39) * mm});
            skLineSegment(sketch, "E21.43.2", {"start": v(-47.52, -38.24) * mm, "end": v(-47.4, -38.39) * mm});
            skLineSegment(sketch, "E21.43.3", {"start": v(-46.29, -36.18) * mm, "end": v(-47.52, -38.24) * mm});
            skLineSegment(sketch, "E21.44.0", {"start": v(-42.98, -40.06) * mm, "end": v(-45.2, -40.96) * mm});
            skLineSegment(sketch, "E21.44.1", {"start": v(-45.2, -40.96) * mm, "end": v(-45.33, -40.82) * mm});
            skLineSegment(sketch, "E21.44.2", {"start": v(-45.46, -40.68) * mm, "end": v(-45.33, -40.82) * mm});
            skLineSegment(sketch, "E21.44.3", {"start": v(-44.33, -38.56) * mm, "end": v(-45.46, -40.68) * mm});
            skLineSegment(sketch, "E21.45.0", {"start": v(-40.82, -42.25) * mm, "end": v(-43, -43.27) * mm});
            skLineSegment(sketch, "E21.45.1", {"start": v(-43, -43.27) * mm, "end": v(-43.13, -43.13) * mm});
            skLineSegment(sketch, "E21.45.2", {"start": v(-43.27, -43) * mm, "end": v(-43.13, -43.13) * mm});
            skLineSegment(sketch, "E21.45.3", {"start": v(-42.25, -40.82) * mm, "end": v(-43.27, -43) * mm});
            skLineSegment(sketch, "E21.46.0", {"start": v(-38.56, -44.33) * mm, "end": v(-40.68, -45.46) * mm});
            skLineSegment(sketch, "E21.46.1", {"start": v(-40.68, -45.46) * mm, "end": v(-40.82, -45.33) * mm});
            skLineSegment(sketch, "E21.46.2", {"start": v(-40.96, -45.2) * mm, "end": v(-40.82, -45.33) * mm});
            skLineSegment(sketch, "E21.46.3", {"start": v(-40.06, -42.98) * mm, "end": v(-40.96, -45.2) * mm});
            skLineSegment(sketch, "E21.47.0", {"start": v(-36.18, -46.29) * mm, "end": v(-38.24, -47.52) * mm});
            skLineSegment(sketch, "E21.47.1", {"start": v(-38.24, -47.52) * mm, "end": v(-38.39, -47.4) * mm});
            skLineSegment(sketch, "E21.47.2", {"start": v(-38.53, -47.29) * mm, "end": v(-38.39, -47.4) * mm});
            skLineSegment(sketch, "E21.47.3", {"start": v(-37.75, -45.02) * mm, "end": v(-38.53, -47.29) * mm});
            skLineSegment(sketch, "E21.48.0", {"start": v(-33.71, -48.12) * mm, "end": v(-35.7, -49.46) * mm});
            skLineSegment(sketch, "E21.48.1", {"start": v(-35.7, -49.46) * mm, "end": v(-35.85, -49.35) * mm});
            skLineSegment(sketch, "E21.48.2", {"start": v(-36, -49.24) * mm, "end": v(-35.85, -49.35) * mm});
            skLineSegment(sketch, "E21.48.3", {"start": v(-35.34, -46.93) * mm, "end": v(-36, -49.24) * mm});
            skLineSegment(sketch, "E21.49.0", {"start": v(-31.15, -49.81) * mm, "end": v(-33.07, -51.26) * mm});
            skLineSegment(sketch, "E21.49.1", {"start": v(-33.07, -51.26) * mm, "end": v(-33.22, -51.16) * mm});
            skLineSegment(sketch, "E21.49.2", {"start": v(-33.38, -51.06) * mm, "end": v(-33.22, -51.16) * mm});
            skLineSegment(sketch, "E21.49.3", {"start": v(-32.84, -48.71) * mm, "end": v(-33.38, -51.06) * mm});
            skLineSegment(sketch, "E21.50.0", {"start": v(-28.5, -51.38) * mm, "end": v(-30.34, -52.92) * mm});
            skLineSegment(sketch, "E21.50.1", {"start": v(-30.34, -52.92) * mm, "end": v(-30.5, -52.83) * mm});
            skLineSegment(sketch, "E21.50.2", {"start": v(-30.66, -52.73) * mm, "end": v(-30.5, -52.83) * mm});
            skLineSegment(sketch, "E21.50.3", {"start": v(-30.24, -50.37) * mm, "end": v(-30.66, -52.73) * mm});
            skLineSegment(sketch, "E21.51.0", {"start": v(-25.77, -52.8) * mm, "end": v(-27.53, -54.44) * mm});
            skLineSegment(sketch, "E21.51.1", {"start": v(-27.53, -54.44) * mm, "end": v(-27.7, -54.35) * mm});
            skLineSegment(sketch, "E21.51.2", {"start": v(-27.86, -54.27) * mm, "end": v(-27.7, -54.35) * mm});
            skLineSegment(sketch, "E21.51.3", {"start": v(-27.57, -51.88) * mm, "end": v(-27.86, -54.27) * mm});
            skLineSegment(sketch, "E21.52.0", {"start": v(-22.97, -54.07) * mm, "end": v(-24.64, -55.8) * mm});
            skLineSegment(sketch, "E21.52.1", {"start": v(-24.64, -55.8) * mm, "end": v(-24.81, -55.73) * mm});
            skLineSegment(sketch, "E21.52.2", {"start": v(-24.98, -55.65) * mm, "end": v(-24.81, -55.73) * mm});
            skLineSegment(sketch, "E21.52.3", {"start": v(-24.81, -53.25) * mm, "end": v(-24.98, -55.65) * mm});
            skLineSegment(sketch, "E21.53.0", {"start": v(-20.1, -55.2) * mm, "end": v(-21.69, -57.02) * mm});
            skLineSegment(sketch, "E21.53.1", {"start": v(-21.69, -57.02) * mm, "end": v(-21.86, -56.95) * mm});
            skLineSegment(sketch, "E21.53.2", {"start": v(-22.04, -56.88) * mm, "end": v(-21.86, -56.95) * mm});
            skLineSegment(sketch, "E21.53.3", {"start": v(-22, -54.48) * mm, "end": v(-22.04, -56.88) * mm});
            skLineSegment(sketch, "E21.54.0", {"start": v(-17.2, -56.18) * mm, "end": v(-18.67, -58.07) * mm});
            skLineSegment(sketch, "E21.54.1", {"start": v(-18.67, -58.07) * mm, "end": v(-18.85, -58.01) * mm});
            skLineSegment(sketch, "E21.54.2", {"start": v(-19.03, -57.96) * mm, "end": v(-18.85, -58.01) * mm});
            skLineSegment(sketch, "E21.54.3", {"start": v(-19.11, -55.55) * mm, "end": v(-19.03, -57.96) * mm});
            skLineSegment(sketch, "E21.55.0", {"start": v(-14.23, -57) * mm, "end": v(-15.6, -58.97) * mm});
            skLineSegment(sketch, "E21.55.1", {"start": v(-15.6, -58.97) * mm, "end": v(-15.79, -58.92) * mm});
            skLineSegment(sketch, "E21.55.2", {"start": v(-15.97, -58.87) * mm, "end": v(-15.79, -58.92) * mm});
            skLineSegment(sketch, "E21.55.3", {"start": v(-16.18, -56.48) * mm, "end": v(-15.97, -58.87) * mm});
            skLineSegment(sketch, "E21.56.0", {"start": v(-11.23, -57.67) * mm, "end": v(-12.5, -59.7) * mm});
            skLineSegment(sketch, "E21.56.1", {"start": v(-12.5, -59.7) * mm, "end": v(-12.68, -59.67) * mm});
            skLineSegment(sketch, "E21.56.2", {"start": v(-12.87, -59.63) * mm, "end": v(-12.68, -59.67) * mm});
            skLineSegment(sketch, "E21.56.3", {"start": v(-13.2, -57.25) * mm, "end": v(-12.87, -59.63) * mm});
            skLineSegment(sketch, "E21.57.0", {"start": v(-8.2, -58.18) * mm, "end": v(-9.36, -60.28) * mm});
            skLineSegment(sketch, "E21.57.1", {"start": v(-9.36, -60.28) * mm, "end": v(-9.54, -60.25) * mm});
            skLineSegment(sketch, "E21.57.2", {"start": v(-9.73, -60.22) * mm, "end": v(-9.54, -60.25) * mm});
            skLineSegment(sketch, "E21.57.3", {"start": v(-10.19, -57.86) * mm, "end": v(-9.73, -60.22) * mm});
            skLineSegment(sketch, "E21.58.0", {"start": v(-5.14, -58.53) * mm, "end": v(-6.19, -60.69) * mm});
            skLineSegment(sketch, "E21.58.1", {"start": v(-6.19, -60.69) * mm, "end": v(-6.38, -60.67) * mm});
            skLineSegment(sketch, "E21.58.2", {"start": v(-6.56, -60.65) * mm, "end": v(-6.38, -60.67) * mm});
            skLineSegment(sketch, "E21.58.3", {"start": v(-7.14, -58.31) * mm, "end": v(-6.56, -60.65) * mm});
            skLineSegment(sketch, "E21.59.0", {"start": v(-2.07, -58.71) * mm, "end": v(-3, -60.93) * mm});
            skLineSegment(sketch, "E21.59.1", {"start": v(-3, -60.93) * mm, "end": v(-3.2, -60.92) * mm});
            skLineSegment(sketch, "E21.59.2", {"start": v(-3.38, -60.9) * mm, "end": v(-3.2, -60.92) * mm});
            skLineSegment(sketch, "E21.59.3", {"start": v(-4.08, -58.6) * mm, "end": v(-3.38, -60.9) * mm});
            skLineSegment(sketch, "E21.60.0", {"start": v(1, -58.74) * mm, "end": v(0.19, -61) * mm});
            skLineSegment(sketch, "E21.60.1", {"start": v(0.19, -61) * mm, "end": v(0, -61) * mm});
            skLineSegment(sketch, "E21.60.2", {"start": v(-0.19, -61) * mm, "end": v(0, -61) * mm});
            skLineSegment(sketch, "E21.60.3", {"start": v(-1, -58.74) * mm, "end": v(-0.19, -61) * mm});
            skLineSegment(sketch, "E21.61.0", {"start": v(4.08, -58.6) * mm, "end": v(3.38, -60.9) * mm});
            skLineSegment(sketch, "E21.61.1", {"start": v(3.38, -60.9) * mm, "end": v(3.2, -60.92) * mm});
            skLineSegment(sketch, "E21.61.2", {"start": v(3, -60.93) * mm, "end": v(3.2, -60.92) * mm});
            skLineSegment(sketch, "E21.61.3", {"start": v(2.07, -58.71) * mm, "end": v(3, -60.93) * mm});
            skLineSegment(sketch, "E21.62.0", {"start": v(7.14, -58.31) * mm, "end": v(6.56, -60.65) * mm});
            skLineSegment(sketch, "E21.62.1", {"start": v(6.56, -60.65) * mm, "end": v(6.38, -60.67) * mm});
            skLineSegment(sketch, "E21.62.2", {"start": v(6.19, -60.69) * mm, "end": v(6.38, -60.67) * mm});
            skLineSegment(sketch, "E21.62.3", {"start": v(5.14, -58.53) * mm, "end": v(6.19, -60.69) * mm});
            skLineSegment(sketch, "E21.63.0", {"start": v(10.19, -57.86) * mm, "end": v(9.73, -60.22) * mm});
            skLineSegment(sketch, "E21.63.1", {"start": v(9.73, -60.22) * mm, "end": v(9.54, -60.25) * mm});
            skLineSegment(sketch, "E21.63.2", {"start": v(9.36, -60.28) * mm, "end": v(9.54, -60.25) * mm});
            skLineSegment(sketch, "E21.63.3", {"start": v(8.2, -58.18) * mm, "end": v(9.36, -60.28) * mm});
            skLineSegment(sketch, "E21.64.0", {"start": v(13.2, -57.25) * mm, "end": v(12.87, -59.63) * mm});
            skLineSegment(sketch, "E21.64.1", {"start": v(12.87, -59.63) * mm, "end": v(12.68, -59.67) * mm});
            skLineSegment(sketch, "E21.64.2", {"start": v(12.5, -59.7) * mm, "end": v(12.68, -59.67) * mm});
            skLineSegment(sketch, "E21.64.3", {"start": v(11.23, -57.67) * mm, "end": v(12.5, -59.7) * mm});
            skLineSegment(sketch, "E21.65.0", {"start": v(16.18, -56.48) * mm, "end": v(15.97, -58.87) * mm});
            skLineSegment(sketch, "E21.65.1", {"start": v(15.97, -58.87) * mm, "end": v(15.79, -58.92) * mm});
            skLineSegment(sketch, "E21.65.2", {"start": v(15.6, -58.97) * mm, "end": v(15.79, -58.92) * mm});
            skLineSegment(sketch, "E21.65.3", {"start": v(14.23, -57) * mm, "end": v(15.6, -58.97) * mm});
            skLineSegment(sketch, "E21.66.0", {"start": v(19.11, -55.55) * mm, "end": v(19.03, -57.96) * mm});
            skLineSegment(sketch, "E21.66.1", {"start": v(19.03, -57.96) * mm, "end": v(18.85, -58.01) * mm});
            skLineSegment(sketch, "E21.66.2", {"start": v(18.67, -58.07) * mm, "end": v(18.85, -58.01) * mm});
            skLineSegment(sketch, "E21.66.3", {"start": v(17.2, -56.18) * mm, "end": v(18.67, -58.07) * mm});
            skLineSegment(sketch, "E21.67.0", {"start": v(22, -54.48) * mm, "end": v(22.04, -56.88) * mm});
            skLineSegment(sketch, "E21.67.1", {"start": v(22.04, -56.88) * mm, "end": v(21.86, -56.95) * mm});
            skLineSegment(sketch, "E21.67.2", {"start": v(21.69, -57.02) * mm, "end": v(21.86, -56.95) * mm});
            skLineSegment(sketch, "E21.67.3", {"start": v(20.1, -55.2) * mm, "end": v(21.69, -57.02) * mm});
            skLineSegment(sketch, "E21.68.0", {"start": v(24.81, -53.25) * mm, "end": v(24.98, -55.65) * mm});
            skLineSegment(sketch, "E21.68.1", {"start": v(24.98, -55.65) * mm, "end": v(24.81, -55.73) * mm});
            skLineSegment(sketch, "E21.68.2", {"start": v(24.64, -55.8) * mm, "end": v(24.81, -55.73) * mm});
            skLineSegment(sketch, "E21.68.3", {"start": v(22.97, -54.07) * mm, "end": v(24.64, -55.8) * mm});
            skLineSegment(sketch, "E21.69.0", {"start": v(27.57, -51.88) * mm, "end": v(27.86, -54.27) * mm});
            skLineSegment(sketch, "E21.69.1", {"start": v(27.86, -54.27) * mm, "end": v(27.7, -54.35) * mm});
            skLineSegment(sketch, "E21.69.2", {"start": v(27.53, -54.44) * mm, "end": v(27.7, -54.35) * mm});
            skLineSegment(sketch, "E21.69.3", {"start": v(25.77, -52.8) * mm, "end": v(27.53, -54.44) * mm});
            skLineSegment(sketch, "E21.70.0", {"start": v(30.24, -50.37) * mm, "end": v(30.66, -52.73) * mm});
            skLineSegment(sketch, "E21.70.1", {"start": v(30.66, -52.73) * mm, "end": v(30.5, -52.83) * mm});
            skLineSegment(sketch, "E21.70.2", {"start": v(30.34, -52.92) * mm, "end": v(30.5, -52.83) * mm});
            skLineSegment(sketch, "E21.70.3", {"start": v(28.5, -51.38) * mm, "end": v(30.34, -52.92) * mm});
            skLineSegment(sketch, "E21.71.0", {"start": v(32.84, -48.71) * mm, "end": v(33.38, -51.06) * mm});
            skLineSegment(sketch, "E21.71.1", {"start": v(33.38, -51.06) * mm, "end": v(33.22, -51.16) * mm});
            skLineSegment(sketch, "E21.71.2", {"start": v(33.07, -51.26) * mm, "end": v(33.22, -51.16) * mm});
            skLineSegment(sketch, "E21.71.3", {"start": v(31.15, -49.81) * mm, "end": v(33.07, -51.26) * mm});
            skLineSegment(sketch, "E21.72.0", {"start": v(35.34, -46.93) * mm, "end": v(36, -49.24) * mm});
            skLineSegment(sketch, "E21.72.1", {"start": v(36, -49.24) * mm, "end": v(35.85, -49.35) * mm});
            skLineSegment(sketch, "E21.72.2", {"start": v(35.7, -49.46) * mm, "end": v(35.85, -49.35) * mm});
            skLineSegment(sketch, "E21.72.3", {"start": v(33.71, -48.12) * mm, "end": v(35.7, -49.46) * mm});
            skLineSegment(sketch, "E21.73.0", {"start": v(37.75, -45.02) * mm, "end": v(38.53, -47.29) * mm});
            skLineSegment(sketch, "E21.73.1", {"start": v(38.53, -47.29) * mm, "end": v(38.39, -47.4) * mm});
            skLineSegment(sketch, "E21.73.2", {"start": v(38.24, -47.52) * mm, "end": v(38.39, -47.4) * mm});
            skLineSegment(sketch, "E21.73.3", {"start": v(36.18, -46.29) * mm, "end": v(38.24, -47.52) * mm});
            skLineSegment(sketch, "E21.74.0", {"start": v(40.06, -42.98) * mm, "end": v(40.96, -45.2) * mm});
            skLineSegment(sketch, "E21.74.1", {"start": v(40.96, -45.2) * mm, "end": v(40.82, -45.33) * mm});
            skLineSegment(sketch, "E21.74.2", {"start": v(40.68, -45.46) * mm, "end": v(40.82, -45.33) * mm});
            skLineSegment(sketch, "E21.74.3", {"start": v(38.56, -44.33) * mm, "end": v(40.68, -45.46) * mm});
            skLineSegment(sketch, "E21.75.0", {"start": v(42.25, -40.82) * mm, "end": v(43.27, -43) * mm});
            skLineSegment(sketch, "E21.75.1", {"start": v(43.27, -43) * mm, "end": v(43.13, -43.13) * mm});
            skLineSegment(sketch, "E21.75.2", {"start": v(43, -43.27) * mm, "end": v(43.13, -43.13) * mm});
            skLineSegment(sketch, "E21.75.3", {"start": v(40.82, -42.25) * mm, "end": v(43, -43.27) * mm});
            skLineSegment(sketch, "E21.76.0", {"start": v(44.33, -38.56) * mm, "end": v(45.46, -40.68) * mm});
            skLineSegment(sketch, "E21.76.1", {"start": v(45.46, -40.68) * mm, "end": v(45.33, -40.82) * mm});
            skLineSegment(sketch, "E21.76.2", {"start": v(45.2, -40.96) * mm, "end": v(45.33, -40.82) * mm});
            skLineSegment(sketch, "E21.76.3", {"start": v(42.98, -40.06) * mm, "end": v(45.2, -40.96) * mm});
            skLineSegment(sketch, "E21.77.0", {"start": v(46.29, -36.18) * mm, "end": v(47.52, -38.24) * mm});
            skLineSegment(sketch, "E21.77.1", {"start": v(47.52, -38.24) * mm, "end": v(47.4, -38.39) * mm});
            skLineSegment(sketch, "E21.77.2", {"start": v(47.29, -38.53) * mm, "end": v(47.4, -38.39) * mm});
            skLineSegment(sketch, "E21.77.3", {"start": v(45.02, -37.75) * mm, "end": v(47.29, -38.53) * mm});
            skLineSegment(sketch, "E21.78.0", {"start": v(48.12, -33.71) * mm, "end": v(49.46, -35.7) * mm});
            skLineSegment(sketch, "E21.78.1", {"start": v(49.46, -35.7) * mm, "end": v(49.35, -35.85) * mm});
            skLineSegment(sketch, "E21.78.2", {"start": v(49.24, -36) * mm, "end": v(49.35, -35.85) * mm});
            skLineSegment(sketch, "E21.78.3", {"start": v(46.93, -35.34) * mm, "end": v(49.24, -36) * mm});
            skLineSegment(sketch, "E21.79.0", {"start": v(49.81, -31.15) * mm, "end": v(51.26, -33.07) * mm});
            skLineSegment(sketch, "E21.79.1", {"start": v(51.26, -33.07) * mm, "end": v(51.16, -33.22) * mm});
            skLineSegment(sketch, "E21.79.2", {"start": v(51.06, -33.38) * mm, "end": v(51.16, -33.22) * mm});
            skLineSegment(sketch, "E21.79.3", {"start": v(48.71, -32.84) * mm, "end": v(51.06, -33.38) * mm});
            skLineSegment(sketch, "E21.80.0", {"start": v(51.38, -28.5) * mm, "end": v(52.92, -30.34) * mm});
            skLineSegment(sketch, "E21.80.1", {"start": v(52.92, -30.34) * mm, "end": v(52.83, -30.5) * mm});
            skLineSegment(sketch, "E21.80.2", {"start": v(52.73, -30.66) * mm, "end": v(52.83, -30.5) * mm});
            skLineSegment(sketch, "E21.80.3", {"start": v(50.37, -30.24) * mm, "end": v(52.73, -30.66) * mm});
            skLineSegment(sketch, "E21.81.0", {"start": v(52.8, -25.77) * mm, "end": v(54.44, -27.53) * mm});
            skLineSegment(sketch, "E21.81.1", {"start": v(54.44, -27.53) * mm, "end": v(54.35, -27.7) * mm});
            skLineSegment(sketch, "E21.81.2", {"start": v(54.27, -27.86) * mm, "end": v(54.35, -27.7) * mm});
            skLineSegment(sketch, "E21.81.3", {"start": v(51.88, -27.57) * mm, "end": v(54.27, -27.86) * mm});
            skLineSegment(sketch, "E21.82.0", {"start": v(54.07, -22.97) * mm, "end": v(55.8, -24.64) * mm});
            skLineSegment(sketch, "E21.82.1", {"start": v(55.8, -24.64) * mm, "end": v(55.73, -24.81) * mm});
            skLineSegment(sketch, "E21.82.2", {"start": v(55.65, -24.98) * mm, "end": v(55.73, -24.81) * mm});
            skLineSegment(sketch, "E21.82.3", {"start": v(53.25, -24.81) * mm, "end": v(55.65, -24.98) * mm});
            skLineSegment(sketch, "E21.83.0", {"start": v(55.2, -20.1) * mm, "end": v(57.02, -21.69) * mm});
            skLineSegment(sketch, "E21.83.1", {"start": v(57.02, -21.69) * mm, "end": v(56.95, -21.86) * mm});
            skLineSegment(sketch, "E21.83.2", {"start": v(56.88, -22.04) * mm, "end": v(56.95, -21.86) * mm});
            skLineSegment(sketch, "E21.83.3", {"start": v(54.48, -22) * mm, "end": v(56.88, -22.04) * mm});
            skLineSegment(sketch, "E21.84.0", {"start": v(56.18, -17.2) * mm, "end": v(58.07, -18.67) * mm});
            skLineSegment(sketch, "E21.84.1", {"start": v(58.07, -18.67) * mm, "end": v(58.01, -18.85) * mm});
            skLineSegment(sketch, "E21.84.2", {"start": v(57.96, -19.03) * mm, "end": v(58.01, -18.85) * mm});
            skLineSegment(sketch, "E21.84.3", {"start": v(55.55, -19.11) * mm, "end": v(57.96, -19.03) * mm});
            skLineSegment(sketch, "E21.85.0", {"start": v(57, -14.23) * mm, "end": v(58.97, -15.6) * mm});
            skLineSegment(sketch, "E21.85.1", {"start": v(58.97, -15.6) * mm, "end": v(58.92, -15.79) * mm});
            skLineSegment(sketch, "E21.85.2", {"start": v(58.87, -15.97) * mm, "end": v(58.92, -15.79) * mm});
            skLineSegment(sketch, "E21.85.3", {"start": v(56.48, -16.18) * mm, "end": v(58.87, -15.97) * mm});
            skLineSegment(sketch, "E21.86.0", {"start": v(57.67, -11.23) * mm, "end": v(59.7, -12.5) * mm});
            skLineSegment(sketch, "E21.86.1", {"start": v(59.7, -12.5) * mm, "end": v(59.67, -12.68) * mm});
            skLineSegment(sketch, "E21.86.2", {"start": v(59.63, -12.87) * mm, "end": v(59.67, -12.68) * mm});
            skLineSegment(sketch, "E21.86.3", {"start": v(57.25, -13.2) * mm, "end": v(59.63, -12.87) * mm});
            skLineSegment(sketch, "E21.87.0", {"start": v(58.18, -8.2) * mm, "end": v(60.28, -9.36) * mm});
            skLineSegment(sketch, "E21.87.1", {"start": v(60.28, -9.36) * mm, "end": v(60.25, -9.54) * mm});
            skLineSegment(sketch, "E21.87.2", {"start": v(60.22, -9.73) * mm, "end": v(60.25, -9.54) * mm});
            skLineSegment(sketch, "E21.87.3", {"start": v(57.86, -10.19) * mm, "end": v(60.22, -9.73) * mm});
            skLineSegment(sketch, "E21.88.0", {"start": v(58.53, -5.14) * mm, "end": v(60.69, -6.19) * mm});
            skLineSegment(sketch, "E21.88.1", {"start": v(60.69, -6.19) * mm, "end": v(60.67, -6.38) * mm});
            skLineSegment(sketch, "E21.88.2", {"start": v(60.65, -6.56) * mm, "end": v(60.67, -6.38) * mm});
            skLineSegment(sketch, "E21.88.3", {"start": v(58.31, -7.14) * mm, "end": v(60.65, -6.56) * mm});
            skLineSegment(sketch, "E21.89.0", {"start": v(58.71, -2.07) * mm, "end": v(60.93, -3) * mm});
            skLineSegment(sketch, "E21.89.1", {"start": v(60.93, -3) * mm, "end": v(60.92, -3.2) * mm});
            skLineSegment(sketch, "E21.89.2", {"start": v(60.9, -3.38) * mm, "end": v(60.92, -3.2) * mm});
            skLineSegment(sketch, "E21.89.3", {"start": v(58.6, -4.08) * mm, "end": v(60.9, -3.38) * mm});
            skLineSegment(sketch, "E21.90.0", {"start": v(58.74, 1) * mm, "end": v(61, 0.19) * mm});
            skLineSegment(sketch, "E21.90.1", {"start": v(61, 0.19) * mm, "end": v(61, 0) * mm});
            skLineSegment(sketch, "E21.90.2", {"start": v(61, -0.19) * mm, "end": v(61, 0) * mm});
            skLineSegment(sketch, "E21.90.3", {"start": v(58.74, -1) * mm, "end": v(61, -0.19) * mm});
            skLineSegment(sketch, "E21.91.0", {"start": v(58.6, 4.08) * mm, "end": v(60.9, 3.38) * mm});
            skLineSegment(sketch, "E21.91.1", {"start": v(60.9, 3.38) * mm, "end": v(60.92, 3.2) * mm});
            skLineSegment(sketch, "E21.91.2", {"start": v(60.93, 3) * mm, "end": v(60.92, 3.2) * mm});
            skLineSegment(sketch, "E21.91.3", {"start": v(58.71, 2.07) * mm, "end": v(60.93, 3) * mm});
            skLineSegment(sketch, "E21.92.0", {"start": v(58.31, 7.14) * mm, "end": v(60.65, 6.56) * mm});
            skLineSegment(sketch, "E21.92.1", {"start": v(60.65, 6.56) * mm, "end": v(60.67, 6.38) * mm});
            skLineSegment(sketch, "E21.92.2", {"start": v(60.69, 6.19) * mm, "end": v(60.67, 6.38) * mm});
            skLineSegment(sketch, "E21.92.3", {"start": v(58.53, 5.14) * mm, "end": v(60.69, 6.19) * mm});
            skLineSegment(sketch, "E21.93.0", {"start": v(57.86, 10.19) * mm, "end": v(60.22, 9.73) * mm});
            skLineSegment(sketch, "E21.93.1", {"start": v(60.22, 9.73) * mm, "end": v(60.25, 9.54) * mm});
            skLineSegment(sketch, "E21.93.2", {"start": v(60.28, 9.36) * mm, "end": v(60.25, 9.54) * mm});
            skLineSegment(sketch, "E21.93.3", {"start": v(58.18, 8.2) * mm, "end": v(60.28, 9.36) * mm});
            skLineSegment(sketch, "E21.94.0", {"start": v(57.25, 13.2) * mm, "end": v(59.63, 12.87) * mm});
            skLineSegment(sketch, "E21.94.1", {"start": v(59.63, 12.87) * mm, "end": v(59.67, 12.68) * mm});
            skLineSegment(sketch, "E21.94.2", {"start": v(59.7, 12.5) * mm, "end": v(59.67, 12.68) * mm});
            skLineSegment(sketch, "E21.94.3", {"start": v(57.67, 11.23) * mm, "end": v(59.7, 12.5) * mm});
            skLineSegment(sketch, "E21.95.0", {"start": v(56.48, 16.18) * mm, "end": v(58.87, 15.97) * mm});
            skLineSegment(sketch, "E21.95.1", {"start": v(58.87, 15.97) * mm, "end": v(58.92, 15.79) * mm});
            skLineSegment(sketch, "E21.95.2", {"start": v(58.97, 15.6) * mm, "end": v(58.92, 15.79) * mm});
            skLineSegment(sketch, "E21.95.3", {"start": v(57, 14.23) * mm, "end": v(58.97, 15.6) * mm});
            skLineSegment(sketch, "E21.96.0", {"start": v(55.55, 19.11) * mm, "end": v(57.96, 19.03) * mm});
            skLineSegment(sketch, "E21.96.1", {"start": v(57.96, 19.03) * mm, "end": v(58.01, 18.85) * mm});
            skLineSegment(sketch, "E21.96.2", {"start": v(58.07, 18.67) * mm, "end": v(58.01, 18.85) * mm});
            skLineSegment(sketch, "E21.96.3", {"start": v(56.18, 17.2) * mm, "end": v(58.07, 18.67) * mm});
            skLineSegment(sketch, "E21.97.0", {"start": v(54.48, 22) * mm, "end": v(56.88, 22.04) * mm});
            skLineSegment(sketch, "E21.97.1", {"start": v(56.88, 22.04) * mm, "end": v(56.95, 21.86) * mm});
            skLineSegment(sketch, "E21.97.2", {"start": v(57.02, 21.69) * mm, "end": v(56.95, 21.86) * mm});
            skLineSegment(sketch, "E21.97.3", {"start": v(55.2, 20.1) * mm, "end": v(57.02, 21.69) * mm});
            skLineSegment(sketch, "E21.98.0", {"start": v(53.25, 24.81) * mm, "end": v(55.65, 24.98) * mm});
            skLineSegment(sketch, "E21.98.1", {"start": v(55.65, 24.98) * mm, "end": v(55.73, 24.81) * mm});
            skLineSegment(sketch, "E21.98.2", {"start": v(55.8, 24.64) * mm, "end": v(55.73, 24.81) * mm});
            skLineSegment(sketch, "E21.98.3", {"start": v(54.07, 22.97) * mm, "end": v(55.8, 24.64) * mm});
            skLineSegment(sketch, "E21.99.0", {"start": v(51.88, 27.57) * mm, "end": v(54.27, 27.86) * mm});
            skLineSegment(sketch, "E21.99.1", {"start": v(54.27, 27.86) * mm, "end": v(54.35, 27.7) * mm});
            skLineSegment(sketch, "E21.99.2", {"start": v(54.44, 27.53) * mm, "end": v(54.35, 27.7) * mm});
            skLineSegment(sketch, "E21.99.3", {"start": v(52.8, 25.77) * mm, "end": v(54.44, 27.53) * mm});
            skLineSegment(sketch, "E21.100.0", {"start": v(50.37, 30.24) * mm, "end": v(52.73, 30.66) * mm});
            skLineSegment(sketch, "E21.100.1", {"start": v(52.73, 30.66) * mm, "end": v(52.83, 30.5) * mm});
            skLineSegment(sketch, "E21.100.2", {"start": v(52.92, 30.34) * mm, "end": v(52.83, 30.5) * mm});
            skLineSegment(sketch, "E21.100.3", {"start": v(51.38, 28.5) * mm, "end": v(52.92, 30.34) * mm});
            skLineSegment(sketch, "E21.101.0", {"start": v(48.71, 32.84) * mm, "end": v(51.06, 33.38) * mm});
            skLineSegment(sketch, "E21.101.1", {"start": v(51.06, 33.38) * mm, "end": v(51.16, 33.22) * mm});
            skLineSegment(sketch, "E21.101.2", {"start": v(51.26, 33.07) * mm, "end": v(51.16, 33.22) * mm});
            skLineSegment(sketch, "E21.101.3", {"start": v(49.81, 31.15) * mm, "end": v(51.26, 33.07) * mm});
            skLineSegment(sketch, "E21.102.0", {"start": v(46.93, 35.34) * mm, "end": v(49.24, 36) * mm});
            skLineSegment(sketch, "E21.102.1", {"start": v(49.24, 36) * mm, "end": v(49.35, 35.85) * mm});
            skLineSegment(sketch, "E21.102.2", {"start": v(49.46, 35.7) * mm, "end": v(49.35, 35.85) * mm});
            skLineSegment(sketch, "E21.102.3", {"start": v(48.12, 33.71) * mm, "end": v(49.46, 35.7) * mm});
            skLineSegment(sketch, "E21.103.0", {"start": v(45.02, 37.75) * mm, "end": v(47.29, 38.53) * mm});
            skLineSegment(sketch, "E21.103.1", {"start": v(47.29, 38.53) * mm, "end": v(47.4, 38.39) * mm});
            skLineSegment(sketch, "E21.103.2", {"start": v(47.52, 38.24) * mm, "end": v(47.4, 38.39) * mm});
            skLineSegment(sketch, "E21.103.3", {"start": v(46.29, 36.18) * mm, "end": v(47.52, 38.24) * mm});
            skLineSegment(sketch, "E21.104.0", {"start": v(42.98, 40.06) * mm, "end": v(45.2, 40.96) * mm});
            skLineSegment(sketch, "E21.104.1", {"start": v(45.2, 40.96) * mm, "end": v(45.33, 40.82) * mm});
            skLineSegment(sketch, "E21.104.2", {"start": v(45.46, 40.68) * mm, "end": v(45.33, 40.82) * mm});
            skLineSegment(sketch, "E21.104.3", {"start": v(44.33, 38.56) * mm, "end": v(45.46, 40.68) * mm});
            skLineSegment(sketch, "E21.105.0", {"start": v(40.82, 42.25) * mm, "end": v(43, 43.27) * mm});
            skLineSegment(sketch, "E21.105.1", {"start": v(43, 43.27) * mm, "end": v(43.13, 43.13) * mm});
            skLineSegment(sketch, "E21.105.2", {"start": v(43.27, 43) * mm, "end": v(43.13, 43.13) * mm});
            skLineSegment(sketch, "E21.105.3", {"start": v(42.25, 40.82) * mm, "end": v(43.27, 43) * mm});
            skLineSegment(sketch, "E21.106.0", {"start": v(38.56, 44.33) * mm, "end": v(40.68, 45.46) * mm});
            skLineSegment(sketch, "E21.106.1", {"start": v(40.68, 45.46) * mm, "end": v(40.82, 45.33) * mm});
            skLineSegment(sketch, "E21.106.2", {"start": v(40.96, 45.2) * mm, "end": v(40.82, 45.33) * mm});
            skLineSegment(sketch, "E21.106.3", {"start": v(40.06, 42.98) * mm, "end": v(40.96, 45.2) * mm});
            skLineSegment(sketch, "E21.107.0", {"start": v(36.18, 46.29) * mm, "end": v(38.24, 47.52) * mm});
            skLineSegment(sketch, "E21.107.1", {"start": v(38.24, 47.52) * mm, "end": v(38.39, 47.4) * mm});
            skLineSegment(sketch, "E21.107.2", {"start": v(38.53, 47.29) * mm, "end": v(38.39, 47.4) * mm});
            skLineSegment(sketch, "E21.107.3", {"start": v(37.75, 45.02) * mm, "end": v(38.53, 47.29) * mm});
            skLineSegment(sketch, "E21.108.0", {"start": v(33.71, 48.12) * mm, "end": v(35.7, 49.46) * mm});
            skLineSegment(sketch, "E21.108.1", {"start": v(35.7, 49.46) * mm, "end": v(35.85, 49.35) * mm});
            skLineSegment(sketch, "E21.108.2", {"start": v(36, 49.24) * mm, "end": v(35.85, 49.35) * mm});
            skLineSegment(sketch, "E21.108.3", {"start": v(35.34, 46.93) * mm, "end": v(36, 49.24) * mm});
            skLineSegment(sketch, "E21.109.0", {"start": v(31.15, 49.81) * mm, "end": v(33.07, 51.26) * mm});
            skLineSegment(sketch, "E21.109.1", {"start": v(33.07, 51.26) * mm, "end": v(33.22, 51.16) * mm});
            skLineSegment(sketch, "E21.109.2", {"start": v(33.38, 51.06) * mm, "end": v(33.22, 51.16) * mm});
            skLineSegment(sketch, "E21.109.3", {"start": v(32.84, 48.71) * mm, "end": v(33.38, 51.06) * mm});
            skLineSegment(sketch, "E21.110.0", {"start": v(28.5, 51.38) * mm, "end": v(30.34, 52.92) * mm});
            skLineSegment(sketch, "E21.110.1", {"start": v(30.34, 52.92) * mm, "end": v(30.5, 52.83) * mm});
            skLineSegment(sketch, "E21.110.2", {"start": v(30.66, 52.73) * mm, "end": v(30.5, 52.83) * mm});
            skLineSegment(sketch, "E21.110.3", {"start": v(30.24, 50.37) * mm, "end": v(30.66, 52.73) * mm});
            skLineSegment(sketch, "E21.111.0", {"start": v(25.77, 52.8) * mm, "end": v(27.53, 54.44) * mm});
            skLineSegment(sketch, "E21.111.1", {"start": v(27.53, 54.44) * mm, "end": v(27.7, 54.35) * mm});
            skLineSegment(sketch, "E21.111.2", {"start": v(27.86, 54.27) * mm, "end": v(27.7, 54.35) * mm});
            skLineSegment(sketch, "E21.111.3", {"start": v(27.57, 51.88) * mm, "end": v(27.86, 54.27) * mm});
            skLineSegment(sketch, "E21.112.0", {"start": v(22.97, 54.07) * mm, "end": v(24.64, 55.8) * mm});
            skLineSegment(sketch, "E21.112.1", {"start": v(24.64, 55.8) * mm, "end": v(24.81, 55.73) * mm});
            skLineSegment(sketch, "E21.112.2", {"start": v(24.98, 55.65) * mm, "end": v(24.81, 55.73) * mm});
            skLineSegment(sketch, "E21.112.3", {"start": v(24.81, 53.25) * mm, "end": v(24.98, 55.65) * mm});
            skLineSegment(sketch, "E21.113.0", {"start": v(20.1, 55.2) * mm, "end": v(21.69, 57.02) * mm});
            skLineSegment(sketch, "E21.113.1", {"start": v(21.69, 57.02) * mm, "end": v(21.86, 56.95) * mm});
            skLineSegment(sketch, "E21.113.2", {"start": v(22.04, 56.88) * mm, "end": v(21.86, 56.95) * mm});
            skLineSegment(sketch, "E21.113.3", {"start": v(22, 54.48) * mm, "end": v(22.04, 56.88) * mm});
            skLineSegment(sketch, "E21.114.0", {"start": v(17.2, 56.18) * mm, "end": v(18.67, 58.07) * mm});
            skLineSegment(sketch, "E21.114.1", {"start": v(18.67, 58.07) * mm, "end": v(18.85, 58.01) * mm});
            skLineSegment(sketch, "E21.114.2", {"start": v(19.03, 57.96) * mm, "end": v(18.85, 58.01) * mm});
            skLineSegment(sketch, "E21.114.3", {"start": v(19.11, 55.55) * mm, "end": v(19.03, 57.96) * mm});
            skLineSegment(sketch, "E21.115.0", {"start": v(14.23, 57) * mm, "end": v(15.6, 58.97) * mm});
            skLineSegment(sketch, "E21.115.1", {"start": v(15.6, 58.97) * mm, "end": v(15.79, 58.92) * mm});
            skLineSegment(sketch, "E21.115.2", {"start": v(15.97, 58.87) * mm, "end": v(15.79, 58.92) * mm});
            skLineSegment(sketch, "E21.115.3", {"start": v(16.18, 56.48) * mm, "end": v(15.97, 58.87) * mm});
            skLineSegment(sketch, "E21.116.0", {"start": v(11.23, 57.67) * mm, "end": v(12.5, 59.7) * mm});
            skLineSegment(sketch, "E21.116.1", {"start": v(12.5, 59.7) * mm, "end": v(12.68, 59.67) * mm});
            skLineSegment(sketch, "E21.116.2", {"start": v(12.87, 59.63) * mm, "end": v(12.68, 59.67) * mm});
            skLineSegment(sketch, "E21.116.3", {"start": v(13.2, 57.25) * mm, "end": v(12.87, 59.63) * mm});
            skLineSegment(sketch, "E21.117.0", {"start": v(8.2, 58.18) * mm, "end": v(9.36, 60.28) * mm});
            skLineSegment(sketch, "E21.117.1", {"start": v(9.36, 60.28) * mm, "end": v(9.54, 60.25) * mm});
            skLineSegment(sketch, "E21.117.2", {"start": v(9.73, 60.22) * mm, "end": v(9.54, 60.25) * mm});
            skLineSegment(sketch, "E21.117.3", {"start": v(10.19, 57.86) * mm, "end": v(9.73, 60.22) * mm});
            skLineSegment(sketch, "E21.118.0", {"start": v(5.14, 58.53) * mm, "end": v(6.19, 60.69) * mm});
            skLineSegment(sketch, "E21.118.1", {"start": v(6.19, 60.69) * mm, "end": v(6.38, 60.67) * mm});
            skLineSegment(sketch, "E21.118.2", {"start": v(6.56, 60.65) * mm, "end": v(6.38, 60.67) * mm});
            skLineSegment(sketch, "E21.118.3", {"start": v(7.14, 58.31) * mm, "end": v(6.56, 60.65) * mm});
            skLineSegment(sketch, "E21.119.0", {"start": v(2.07, 58.71) * mm, "end": v(3, 60.93) * mm});
            skLineSegment(sketch, "E21.119.1", {"start": v(3, 60.93) * mm, "end": v(3.2, 60.92) * mm});
            skLineSegment(sketch, "E21.119.2", {"start": v(3.38, 60.9) * mm, "end": v(3.2, 60.92) * mm});
            skLineSegment(sketch, "E21.119.3", {"start": v(4.08, 58.6) * mm, "end": v(3.38, 60.9) * mm});
            skCircle(sketch, "E22", {"center": v(0, 0) * mm, "radius": 7.5 * mm});
            skSolve(sketch);
        }
        {
            var Q0;
            Q0=qSketchRegion(id+"F4",true);
            extrude(context, id + "F5", {"entities" : qUnion([Q0]), "operationType" : NewBodyOperationType.ADD, "depth" : 10 * mm});
        }
        {
            var Q0;
            Q0=makeQuery(id+"F3.opExtrude","SWEPT_FACE",FACE,{"disambiguationData":[OSD([sQuery(id+"F2.wireOp",EDGE,"E13.top")])]});
            var sketch = newSketch(context, id + "F6", { "sketchPlane" : qUnion([Q0])});
            skLineSegment(sketch, "E23", {"start": v(0, 20) * mm, "end": v(0, 10) * mm, "construction": true});
            skPoint(sketch, "E23.endSnap0", {"position": v(-25, 10) * mm});
            skCircle(sketch, "E24", {"center": v(0, 10) * mm, "radius": 0.5 * mm});
            skSolve(sketch);
        }
        {
            var Q0;
            Q0=qSketchRegion(id+"F6",true);
            extrude(context, id + "F7", {"entities" : qUnion([Q0]), "operationType" : NewBodyOperationType.REMOVE, "depth" : -1 * mm});
        }
    });
